FCSTD DOCUMENT  (FreeCAD 0.21R33771 (Git))
Label: MHD-1H
License: All rights reserved
LicenseURL: http://en.wikipedia.org/wiki/All_rights_reserved
objects: Part::Part2DObjectPython×204, App::FeaturePython×31, Part::Feature×23, Part::FeaturePython×14
note: 241 computed .brp shape members not serialized (recipe doc carries the construction recipe); baked Part::Feature solids carry a one-line shape summary decoded from their .brp

FEATURE [Part::Part2DObjectPython] Arc  # Draft 2D object (typed FeaturePython)
  Area = 0
  FirstAngle = -90
  LastAngle = -60.1372
  MakeFace = false
  Placement = pos=(75,95.31,0) rot=(0,0,1;0rad)
  Radius = 75.3125
FEATURE [Part::Part2DObjectPython] Arc001  # Draft 2D object (typed FeaturePython)
  Area = 0
  FirstAngle = -119.863
  LastAngle = -90
  MakeFace = false
  Placement = pos=(-75,95.31,0) rot=(0,0,1;0rad)
  Radius = 75.3125
FEATURE [Part::Part2DObjectPython] Line003  # Draft 2D object (typed FeaturePython)
  Area = 0
  ChamferSize = 0
  Closed = false
  End = (65,-5,0)
  FilletRadius = 0
  Length = 130
  MakeFace = false
  Placement = pos=(-112.523,-5.20498,0) rot=(0,0,1;0rad)
  Points = (2) [(47.5228,0.204983,0),(177.523,0.204983,0)]
  Start = (-65,-5,0)
  Subdivisions = 0
FEATURE [Part::Part2DObjectPython] Line004  # Draft 2D object (typed FeaturePython)
  Area = 0
  ChamferSize = 0
  Closed = false
  End = (75,20,0)
  FilletRadius = 0
  Length = 150
  MakeFace = false
  Placement = pos=(-75,20,0) rot=(0,0,1;0rad)
  Points = (2) [(0,0,0),(150,-7.10543e-15,0)]
  Start = (-75,20,0)
  Subdivisions = 0
FEATURE [Part::Part2DObjectPython] Arc004  # Draft 2D object (typed FeaturePython)
  Area = 0
  FirstAngle = 90
  LastAngle = 119.863
  MakeFace = false
  Placement = pos=(-75,-35.31,0) rot=(0,0,1;0rad)
  Radius = 75.3125
FEATURE [Part::Part2DObjectPython] Arc005  # Draft 2D object (typed FeaturePython)
  Area = 0
  FirstAngle = 60.1372
  LastAngle = 90
  MakeFace = false
  Placement = pos=(75,-35.31,0) rot=(0,0,1;0rad)
  Radius = 75.3125
FEATURE [Part::Part2DObjectPython] Line005  # Draft 2D object (typed FeaturePython)
  Area = 0
  ChamferSize = 0
  Closed = false
  End = (75,40,0)
  FilletRadius = 0
  Length = 150
  MakeFace = false
  Placement = pos=(-75,20,0) rot=(0,0,1;0rad)
  Points = (2) [(0,20,0),(150,20,0)]
  Start = (-75,40,0)
  Subdivisions = 0
FEATURE [Part::Part2DObjectPython] Line006  # Draft 2D object (typed FeaturePython)
  Area = 0
  ChamferSize = 0
  Closed = false
  End = (-142.5,-4.99634,0)
  FilletRadius = 0
  Length = 20
  MakeFace = false
  Placement = pos=(-155.462,-5.16722,0) rot=(0,0,1;0rad)
  Points = (2) [(-7.03764,0.167221,0),(12.9624,0.170881,0)]
  Start = (-162.5,-5,0)
  Subdivisions = 0
FEATURE [Part::Part2DObjectPython] Line010  # Draft 2D object (typed FeaturePython)
  Area = 0
  ChamferSize = 0
  Closed = false
  End = (-152.5,-5,0)
  FilletRadius = 0
  Length = 25
  MakeFace = false
  Points = (2) [(-152.5,-30,0),(-152.5,-5,0)]
  Start = (-152.5,-30,0)
  Subdivisions = 0
FEATURE [Part::Part2DObjectPython] Line020  # Draft 2D object (typed FeaturePython)
  Area = 0
  ChamferSize = 0
  Closed = false
  End = (-71,-39.24,0)
  FilletRadius = 0
  Length = 1
  MakeFace = false
  Placement = pos=(-75,-40,0) rot=(0,0,1;0rad)
  Points = (2) [(3,0.76,0),(4,0.76,0)]
  Start = (-72,-39.24,0)
  Subdivisions = 0
FEATURE [Part::Part2DObjectPython] Line023  # Draft 2D object (typed FeaturePython)
  Area = 0
  ChamferSize = 0
  Closed = false
  End = (-75,-35,0)
  FilletRadius = 0
  Length = 4.5
  MakeFace = false
  Placement = pos=(-75,-40,0) rot=(0,0,1;0rad)
  Points = (2) [(0,0.5,0),(0,5,0)]
  Start = (-75,-39.5,0)
  Subdivisions = 0
FEATURE [Part::Part2DObjectPython] Line024  # Draft 2D object (typed FeaturePython)
  Area = 0
  ChamferSize = 0
  Closed = false
  End = (30,-35,0)
  FilletRadius = 0
  Length = 4.5
  MakeFace = false
  Placement = pos=(-75,-40,0) rot=(0,0,1;0rad)
  Points = (2) [(105,0.5,0),(105,5,0)]
  Start = (30,-39.5,0)
  Subdivisions = 0
FEATURE [Part::Part2DObjectPython] Line028  # Draft 2D object (typed FeaturePython)
  Area = 0
  ChamferSize = 0
  Closed = false
  End = (65,-9.1,0)
  FilletRadius = 0
  Length = 2.2
  MakeFace = false
  Points = (2) [(65,-6.9,0),(65,-9.1,0)]
  Start = (65,-6.9,0)
  Subdivisions = 0
FEATURE [Part::Part2DObjectPython] Line029  # Draft 2D object (typed FeaturePython)
  Area = 0
  ChamferSize = 0
  Closed = false
  End = (36.1,-23,0)
  FilletRadius = 0
  Length = 2.2
  MakeFace = false
  Points = (2) [(33.9,-23,0),(36.1,-23,0)]
  Start = (33.9,-23,0)
  Subdivisions = 0
FEATURE [Part::Part2DObjectPython] Line031  # Draft 2D object (typed FeaturePython)
  Area = 0
  ChamferSize = 0
  Closed = false
  End = (30,20,0)
  FilletRadius = 0
  Length = 20
  MakeFace = false
  Placement = pos=(-75,-40,0) rot=(0,0,1;0rad)
  Points = (2) [(105,80,0),(105,60,0)]
  Start = (30,40,0)
  Subdivisions = 0
FEATURE [Part::Part2DObjectPython] Line032  # Draft 2D object (typed FeaturePython)
  Area = 0
  ChamferSize = 0
  Closed = false
  End = (-65,23.5,0)
  FilletRadius = 0
  Length = 13
  MakeFace = false
  Placement = pos=(-75,-40,0) rot=(0,0,1;0rad)
  Points = (2) [(10,76.5,0),(10,63.5,0)]
  Start = (-65,36.5,0)
  Subdivisions = 0
FEATURE [Part::Part2DObjectPython] Line033  # Draft 2D object (typed FeaturePython)
  Area = 0
  ChamferSize = 0
  Closed = false
  End = (-75,20,0)
  FilletRadius = 0
  Length = 20
  MakeFace = false
  Placement = pos=(-75,-40,0) rot=(0,0,1;0rad)
  Points = (2) [(0,80,0),(0,60,0)]
  Start = (-75,40,0)
  Subdivisions = 0
FEATURE [Part::Part2DObjectPython] Line034  # Draft 2D object (typed FeaturePython)
  Area = 0
  ChamferSize = 0
  Closed = false
  End = (65,23.5,0)
  FilletRadius = 0
  Length = 13
  MakeFace = false
  Placement = pos=(-75,-40,0) rot=(0,0,1;0rad)
  Points = (2) [(140,76.5,0),(140,63.5,0)]
  Start = (65,36.5,0)
  Subdivisions = 0
FEATURE [Part::Part2DObjectPython] Line035  # Draft 2D object (typed FeaturePython)
  Area = 0
  ChamferSize = 0
  Closed = false
  End = (65,36.5,0)
  FilletRadius = 0
  Length = 130
  MakeFace = false
  Placement = pos=(-75,-40,0) rot=(0,0,1;0rad)
  Points = (2) [(10,76.5,0),(140,76.5,0)]
  Start = (-65,36.5,0)
  Subdivisions = 0
FEATURE [Part::Part2DObjectPython] Line036  # Draft 2D object (typed FeaturePython)
  Area = 0
  ChamferSize = 0
  Closed = false
  End = (65,23.5,0)
  FilletRadius = 0
  Length = 130
  MakeFace = false
  Placement = pos=(-75,-40,0) rot=(0,0,1;0rad)
  Points = (2) [(10,63.5,0),(140,63.5,0)]
  Start = (-65,23.5,0)
  Subdivisions = 0
FEATURE [Part::Part2DObjectPython] Line037  # Draft 2D object (typed FeaturePython)
  Area = 0
  ChamferSize = 0
  Closed = false
  End = (75,20,0)
  FilletRadius = 0
  Length = 20
  MakeFace = false
  Placement = pos=(-75,-40,0) rot=(0,0,1;0rad)
  Points = (2) [(150,80,0),(150,60,0)]
  Start = (75,40,0)
  Subdivisions = 0
FEATURE [Part::Part2DObjectPython] Line038  # Draft 2D object (typed FeaturePython)
  Area = 0
  ChamferSize = 0
  Closed = false
  End = (27,23.5,0)
  FilletRadius = 0
  Length = 13.04
  MakeFace = false
  Points = (2) [(27,36.54,0),(27,23.5,0)]
  Start = (27,36.54,0)
  Subdivisions = 0
FEATURE [Part::Part2DObjectPython] Line039  # Draft 2D object (typed FeaturePython)
  Area = 0
  ChamferSize = 0
  Closed = false
  End = (-72,23.5,0)
  FilletRadius = 0
  Length = 13
  MakeFace = false
  Points = (2) [(-72,36.5,0),(-72,23.5,0)]
  Start = (-72,36.5,0)
  Subdivisions = 0
FEATURE [Part::Part2DObjectPython] Line040  # Draft 2D object (typed FeaturePython)
  Area = 0
  ChamferSize = 0
  Closed = false
  End = (-72,23.5,0)
  FilletRadius = 0
  Length = 7
  MakeFace = false
  Placement = pos=(-75,-40,0) rot=(0,0,1;0rad)
  Points = (2) [(10,63.5,0),(3,63.5,0)]
  Start = (-65,23.5,0)
  Subdivisions = 0
FEATURE [Part::Part2DObjectPython] Line041  # Draft 2D object (typed FeaturePython)
  Area = 0
  ChamferSize = 0
  Closed = false
  End = (-72,36.5,0)
  FilletRadius = 0
  Length = 7
  MakeFace = false
  Placement = pos=(-75,-40,0) rot=(0,0,1;0rad)
  Points = (2) [(10,76.5,0),(3,76.5,0)]
  Start = (-65,36.5,0)
  Subdivisions = 0
FEATURE [Part::Part2DObjectPython] Line044  # Draft 2D object (typed FeaturePython)
  Area = 0
  ChamferSize = 0
  Closed = false
  End = (30,39.5,0)
  FilletRadius = 0
  Length = 105
  MakeFace = false
  Placement = pos=(-75,-40,0) rot=(0,0,1;0rad)
  Points = (2) [(0,79.5,0),(105,79.5,0)]
  Start = (-75,39.5,0)
  Subdivisions = 0
FEATURE [Part::Part2DObjectPython] Line045  # Draft 2D object (typed FeaturePython)
  Area = 0
  ChamferSize = 0
  Closed = false
  End = (30,20.5,0)
  FilletRadius = 0
  Length = 105
  MakeFace = false
  Placement = pos=(-75,-40,0) rot=(0,0,1;0rad)
  Points = (2) [(0,60.5,0),(105,60.5,0)]
  Start = (-75,20.5,0)
  Subdivisions = 0
FEATURE [Part::Part2DObjectPython] Line046  # Draft 2D object (typed FeaturePython)
  Area = 0
  ChamferSize = 0
  Closed = false
  End = (30,-35,0)
  FilletRadius = 0
  Length = 105
  MakeFace = false
  Placement = pos=(-75,-40,0) rot=(0,0,1;0rad)
  Points = (2) [(0,5,0),(105,5,0)]
  Start = (-75,-35,0)
  Subdivisions = 0
FEATURE [Part::Part2DObjectPython] Line052  # Draft 2D object (typed FeaturePython)
  Area = 0
  ChamferSize = 0
  Closed = false
  End = (-22,-39.24,0)
  FilletRadius = 0
  Length = 11
  MakeFace = false
  Placement = pos=(-75,-40,0) rot=(0,0,1;0rad)
  Points = (2) [(42,0.76,0),(53,0.76,0)]
  Start = (-33,-39.24,0)
  Subdivisions = 0
FEATURE [Part::Part2DObjectPython] Line053  # Draft 2D object (typed FeaturePython)
  Area = 0
  ChamferSize = 0
  Closed = false
  End = (16,-39.24,0)
  FilletRadius = 0
  Length = 38
  MakeFace = false
  Placement = pos=(-75,-40,0) rot=(0,0,1;0rad)
  Points = (2) [(53,0.76,0),(91,0.76,0)]
  Start = (-22,-39.24,0)
  Subdivisions = 0
FEATURE [Part::Part2DObjectPython] Line054  # Draft 2D object (typed FeaturePython)
  Area = 0
  ChamferSize = 0
  Closed = false
  End = (27,-39.24,0)
  FilletRadius = 0
  Length = 11
  MakeFace = false
  Placement = pos=(-75,-40,0) rot=(0,0,1;0rad)
  Points = (2) [(91,0.76,0),(102,0.76,0)]
  Start = (16,-39.24,0)
  Subdivisions = 0
FEATURE [Part::Part2DObjectPython] Line055  # Draft 2D object (typed FeaturePython)
  Area = 0
  ChamferSize = 0
  Closed = false
  End = (-33,-39.24,0)
  FilletRadius = 0
  Length = 38
  MakeFace = false
  Placement = pos=(-75,-40,0) rot=(0,0,1;0rad)
  Points = (2) [(4,0.76,0),(42,0.76,0)]
  Start = (-71,-39.24,0)
  Subdivisions = 0
FEATURE [Part::Part2DObjectPython] Line064  # Draft 2D object (typed FeaturePython)
  Area = 0
  ChamferSize = 0
  Closed = false
  End = (-146,-23,0)
  FilletRadius = 0
  Length = 13
  MakeFace = false
  Points = (2) [(-159,-23,0),(-146,-23,0)]
  Start = (-159,-23,0)
  Subdivisions = 0
FEATURE [Part::Part2DObjectPython] Line069  # Draft 2D object (typed FeaturePython)
  Area = 0
  ChamferSize = 0
  Closed = false
  End = (-65,-5,0)
  FilletRadius = 0
  Length = 10
  MakeFace = false
  Placement = pos=(-112.523,-5.20498,0) rot=(0,0,1;0rad)
  Points = (2) [(37.5228,0.204983,0),(47.5228,0.204983,0)]
  Start = (-75,-5,0)
  Subdivisions = 0
FEATURE [Part::Part2DObjectPython] Line070  # Draft 2D object (typed FeaturePython)
  Area = 0
  ChamferSize = 0
  Closed = false
  End = (-75,-5.2,0)
  FilletRadius = 0
  Length = 0.2
  MakeFace = false
  Placement = pos=(-112.523,-5.20498,0) rot=(0,0,1;0rad)
  Points = (2) [(37.5228,0.204983,0),(37.5228,0.00498323,0)]
  Start = (-75,-5,0)
  Subdivisions = 0
FEATURE [Part::Part2DObjectPython] Line071  # Draft 2D object (typed FeaturePython)
  Area = 0
  ChamferSize = 0
  Closed = false
  End = (75,-5,0)
  FilletRadius = 0
  Length = 10
  MakeFace = false
  Placement = pos=(-112.523,-5.20498,0) rot=(0,0,1;0rad)
  Points = (2) [(177.523,0.204983,0),(187.523,0.204983,0)]
  Start = (65,-5,0)
  Subdivisions = 0
FEATURE [Part::Part2DObjectPython] Line072  # Draft 2D object (typed FeaturePython)
  Area = 0
  ChamferSize = 0
  Closed = false
  End = (75,-5.2,0)
  FilletRadius = 0
  Length = 0.2
  MakeFace = false
  Placement = pos=(-112.523,-5.20498,0) rot=(0,0,1;0rad)
  Points = (2) [(187.523,0.204983,0),(187.523,0.00498323,0)]
  Start = (75,-5,0)
  Subdivisions = 0
FEATURE [Part::Part2DObjectPython] Line073  # Draft 2D object (typed FeaturePython)
  Area = 0
  ChamferSize = 0
  Closed = false
  End = (-65,-5.2,0)
  FilletRadius = 0
  Length = 0.2
  MakeFace = false
  Points = (2) [(-65,-5,0),(-65,-5.2,0)]
  Start = (-65,-5,0)
  Subdivisions = 0
FEATURE [Part::Part2DObjectPython] Line074  # Draft 2D object (typed FeaturePython)
  Area = 0
  ChamferSize = 0
  Closed = false
  End = (65,-5.2,0)
  FilletRadius = 0
  Length = 0.2
  MakeFace = false
  Points = (2) [(65,-5,0),(65,-5.2,0)]
  Start = (65,-5,0)
  Subdivisions = 0
FEATURE [Part::Part2DObjectPython] Line075  # Draft 2D object (typed FeaturePython)
  Area = 0
  ChamferSize = 0
  Closed = false
  End = (-65,-5.2,0)
  FilletRadius = 0
  Length = 130
  MakeFace = false
  Placement = pos=(-112.523,-5.20498,0) rot=(0,0,1;0rad)
  Points = (2) [(177.523,0.00498323,0),(47.5228,0.00498323,0)]
  Start = (65,-5.2,0)
  Subdivisions = 0
FEATURE [Part::Part2DObjectPython] Line076  # Draft 2D object (typed FeaturePython)
  Area = 0
  ChamferSize = 0
  Closed = true
  End = (-162.5,-5,0)
  FilletRadius = 0
  Length = 30
  MakeFace = false
  Placement = pos=(-112.5,-30,0) rot=(0,0,1;0rad)
  Points = (2) [(-50,25,0),(-50,25,0)]
  Start = (-162.5,-5,0)
  Subdivisions = 0
FEATURE [Part::Part2DObjectPython] Line077  # Draft 2D object (typed FeaturePython)
  Area = 0
  ChamferSize = 0
  Closed = false
  End = (-159,-5,0)
  FilletRadius = 0
  Length = 0.2
  MakeFace = false
  Points = (2) [(-159,-5.2,0),(-159,-5,0)]
  Start = (-159,-5.2,0)
  Subdivisions = 0
FEATURE [Part::Part2DObjectPython] Line078  # Draft 2D object (typed FeaturePython)
  Area = 0
  ChamferSize = 0
  Closed = false
  End = (-146,-5,0)
  FilletRadius = 0
  Length = 0.2
  MakeFace = false
  Points = (2) [(-146,-5.2,0),(-146,-5,0)]
  Start = (-146,-5.2,0)
  Subdivisions = 0
FEATURE [Part::Part2DObjectPython] Line079  # Draft 2D object (typed FeaturePython)
  Area = 0
  ChamferSize = 0
  Closed = false
  End = (-142.5,-5,0)
  FilletRadius = 0
  Length = 0.2
  MakeFace = false
  Placement = pos=(-112.5,-30,0) rot=(0,0,1;0rad)
  Points = (2) [(-30,24.8,0),(-30,25,0)]
  Start = (-142.5,-5.2,0)
  Subdivisions = 0
FEATURE [Part::Part2DObjectPython] Line081  # Draft 2D object (typed FeaturePython)
  Area = 0
  ChamferSize = 0
  Closed = false
  End = (-159,-5.2,0)
  FilletRadius = 0
  Length = 13
  MakeFace = false
  Points = (2) [(-146,-5.2,0),(-159,-5.2,0)]
  Start = (-146,-5.2,0)
  Subdivisions = 0
FEATURE [Part::Part2DObjectPython] Line083  # Draft 2D object (typed FeaturePython)
  Area = 0
  ChamferSize = 0
  Closed = true
  End = (-71,35.5,0)
  FilletRadius = 0
  Length = 11
  MakeFace = false
  Placement = pos=(-157.5,-40,0) rot=(0,0,1;0rad)
  Points = (2) [(86.5,64.5,0),(86.5,75.5,0)]
  Start = (-71,24.5,0)
  Subdivisions = 0
FEATURE [Part::Part2DObjectPython] Line084  # Draft 2D object (typed FeaturePython)
  Area = 0
  ChamferSize = 0
  Closed = true
  End = (-33,35.5,0)
  FilletRadius = 0
  Length = 11
  MakeFace = false
  Placement = pos=(-157.5,-40,0) rot=(0,0,1;0rad)
  Points = (2) [(124.5,64.5,0),(124.5,75.5,0)]
  Start = (-33,24.5,0)
  Subdivisions = 0
FEATURE [Part::Part2DObjectPython] Line087  # Draft 2D object (typed FeaturePython)
  Area = 0
  ChamferSize = 0
  Closed = false
  End = (-33,35.5,0)
  FilletRadius = 0
  Length = 32
  MakeFace = false
  Placement = pos=(-70.9707,35.5939,0) rot=(0,0,1;0rad)
  Points = (2) [(5.97074,-0.0939102,0),(37.9707,-0.0939102,0)]
  Start = (-65,35.5,0)
  Subdivisions = 0
FEATURE [Part::Part2DObjectPython] Line088  # Draft 2D object (typed FeaturePython)
  Area = 0
  ChamferSize = 0
  Closed = false
  End = (-65,35.5,0)
  FilletRadius = 0
  Length = 6
  MakeFace = false
  Placement = pos=(-70.9707,35.5939,0) rot=(0,0,1;0rad)
  Points = (2) [(-0.0292587,-0.0939102,0),(5.97074,-0.0939102,0)]
  Start = (-71,35.5,0)
  Subdivisions = 0
FEATURE [Part::Part2DObjectPython] Line089  # Draft 2D object (typed FeaturePython)
  Area = 0
  ChamferSize = 0
  Closed = false
  End = (-65,24.5,0)
  FilletRadius = 0
  Length = 6
  MakeFace = false
  Placement = pos=(-70.9707,35.5939,0) rot=(0,0,1;0rad)
  Points = (2) [(-0.0292587,-11.0939,0),(5.97074,-11.0939,0)]
  Start = (-71,24.5,0)
  Subdivisions = 0
FEATURE [Part::Part2DObjectPython] Line090  # Draft 2D object (typed FeaturePython)
  Area = 0
  ChamferSize = 0
  Closed = false
  End = (-33,24.5,0)
  FilletRadius = 0
  Length = 32
  MakeFace = false
  Placement = pos=(-70.9707,35.5939,0) rot=(0,0,1;0rad)
  Points = (2) [(5.97074,-11.0939,0),(37.9707,-11.0939,0)]
  Start = (-65,24.5,0)
  Subdivisions = 0
FEATURE [Part::Part2DObjectPython] Line095  # Draft 2D object (typed FeaturePython)
  Area = 0
  ChamferSize = 0
  Closed = true
  End = (35.5,-23,0)
  FilletRadius = 0
  Length = 35.4
  MakeFace = false
  Placement = pos=(35.5,-60,0) rot=(0,0,1;0rad)
  Points = (2) [(0,1.6,0),(0,37,0)]
  Start = (35.5,-58.4,0)
  Subdivisions = 0
FEATURE [Part::Part2DObjectPython] Line096  # Draft 2D object (typed FeaturePython)
  Area = 0
  ChamferSize = 0
  Closed = false
  End = (74.5,-18,0)
  FilletRadius = 0
  Length = 40.4
  MakeFace = false
  Placement = pos=(35.5,-60,0) rot=(0,0,1;0rad)
  Points = (2) [(39,1.6,0),(39,42,0)]
  Start = (74.5,-58.4,0)
  Subdivisions = 0
FEATURE [Part::Part2DObjectPython] Line097  # Draft 2D object (typed FeaturePython)
  Area = 0
  ChamferSize = 0
  Closed = true
  End = (35,-62.2,0)
  FilletRadius = 0
  Length = 0.5
  MakeFace = false
  Placement = pos=(35.5,-60,0) rot=(0,0,1;0rad)
  Points = (2) [(0,-2.2,0),(-0.5,-2.2,0)]
  Start = (35.5,-62.2,0)
  Subdivisions = 0
FEATURE [Part::Part2DObjectPython] Line099  # Draft 2D object (typed FeaturePython)
  Area = 0
  ChamferSize = 0
  Closed = true
  End = (75.5,-18,0)
  FilletRadius = 0
  Length = 43.7
  MakeFace = false
  Placement = pos=(35.5,-60,0) rot=(0,0,1;0rad)
  Points = (2) [(40,-1.7,0),(40,42,0)]
  Start = (75.5,-61.7,0)
  Subdivisions = 0
FEATURE [Part::Part2DObjectPython] Line101  # Draft 2D object (typed FeaturePython)
  Area = 0
  ChamferSize = 0
  Closed = true
  End = (35.5,-62.2,0)
  FilletRadius = 0
  Length = 37
  MakeFace = false
  Placement = pos=(35.5,-60,0) rot=(0,0,1;0rad)
  Points = (2) [(37,-2.2,0),(0,-2.2,0)]
  Start = (72.5,-62.2,0)
  Subdivisions = 0
FEATURE [Part::Part2DObjectPython] Line102  # Draft 2D object (typed FeaturePython)
  Area = 0
  ChamferSize = 0
  Closed = true
  End = (34.5,-23,0)
  FilletRadius = 0
  Length = 38.7
  MakeFace = false
  Placement = pos=(35.5,-60,0) rot=(0,0,1;0rad)
  Points = (2) [(-1,-1.7,0),(-1,37,0)]
  Start = (34.5,-61.7,0)
  Subdivisions = 0
FEATURE [Part::Part2DObjectPython] Arc010  # Draft 2D object (typed FeaturePython)
  Area = 0
  FirstAngle = 0
  LastAngle = 90
  MakeFace = false
  Placement = pos=(27,-23,0) rot=(0,0,1;0rad)
  Radius = 6.9
FEATURE [Part::Part2DObjectPython] Arc011  # Draft 2D object (typed FeaturePython)
  Area = 0
  FirstAngle = 0
  LastAngle = 90
  MakeFace = false
  Placement = pos=(65,-18,0) rot=(0,0,1;0rad)
  Radius = 9.5
FEATURE [Part::Part2DObjectPython] Arc012  # Draft 2D object (typed FeaturePython)
  Area = 0
  FirstAngle = 0
  LastAngle = 90
  MakeFace = false
  Placement = pos=(65,-18,0) rot=(0,0,1;0rad)
  Radius = 10.5
FEATURE [Part::Part2DObjectPython] Arc015  # Draft 2D object (typed FeaturePython)
  Area = 0
  FirstAngle = 0
  LastAngle = 90
  MakeFace = false
  Placement = pos=(27,-23,0) rot=(0,0,1;0rad)
  Radius = 7.5
FEATURE [Part::Part2DObjectPython] Arc016  # Draft 2D object (typed FeaturePython)
  Area = 0
  FirstAngle = 0
  LastAngle = 90
  MakeFace = false
  Placement = pos=(27,-23,0) rot=(0,0,1;0rad)
  Radius = 8.5
FEATURE [Part::Part2DObjectPython] Arc017  # Draft 2D object (typed FeaturePython)
  Area = 0
  FirstAngle = 0
  LastAngle = 90
  MakeFace = false
  Placement = pos=(27,-23,0) rot=(0,0,1;0rad)
  Radius = 9.1
FEATURE [Part::Part2DObjectPython] Arc018  # Draft 2D object (typed FeaturePython)
  Area = 0
  FirstAngle = 90
  LastAngle = 180
  MakeFace = false
  Placement = pos=(35,-61.7,0) rot=(0,0,1;0rad)
  Radius = 0.5
FEATURE [Part::Part2DObjectPython] Arc019  # Draft 2D object (typed FeaturePython)
  Area = 0
  FirstAngle = 180
  LastAngle = 360
  MakeFace = false
  Placement = pos=(35,-61.7,0) rot=(0,0,1;0rad)
  Radius = 0.5
FEATURE [Part::Part2DObjectPython] Line105  # Draft 2D object (typed FeaturePython)
  Area = 0
  ChamferSize = 0
  Closed = true
  End = (35,-61.2,0)
  FilletRadius = 0
  Length = 37.5
  MakeFace = false
  Placement = pos=(35.5,-60,0) rot=(0,0,1;0rad)
  Points = (2) [(37,-1.2,0),(-0.5,-1.2,0)]
  Start = (72.5,-61.2,0)
  Subdivisions = 0
FEATURE [Part::Part2DObjectPython] Line106  # Draft 2D object (typed FeaturePython)
  Area = 0
  ChamferSize = 0
  Closed = true
  End = (71.5,-61.2,0)
  FilletRadius = 0
  Length = 1
  MakeFace = false
  Placement = pos=(35.5,-60,0) rot=(0,0,1;0rad)
  Points = (2) [(36,-2.2,0),(36,-1.2,0)]
  Start = (71.5,-62.2,0)
  Subdivisions = 0
FEATURE [Part::Part2DObjectPython] Arc020  # Draft 2D object (typed FeaturePython)
  Area = 0
  FirstAngle = 180
  LastAngle = 360
  MakeFace = false
  Placement = pos=(75,-61.7,0) rot=(0,0,1;0rad)
  Radius = 0.5
FEATURE [Part::Part2DObjectPython] Line107  # Draft 2D object (typed FeaturePython)
  Area = 0
  ChamferSize = 0
  Closed = true
  End = (72.5,-58.7,0)
  FilletRadius = 0
  Length = 6
  MakeFace = false
  Placement = pos=(35.5,-60,0) rot=(0,0,1;0rad)
  Points = (2) [(37,-4.7,0),(37,1.3,0)]
  Start = (72.5,-64.7,0)
  Subdivisions = 0
FEATURE [Part::Part2DObjectPython] Line108  # Draft 2D object (typed FeaturePython)
  Area = 0
  ChamferSize = 0
  Closed = true
  End = (37.5,-58.7,0)
  FilletRadius = 0
  Length = 6
  MakeFace = false
  Placement = pos=(35.5,-60,0) rot=(0,0,1;0rad)
  Points = (2) [(2,-4.7,0),(2,1.3,0)]
  Start = (37.5,-64.7,0)
  Subdivisions = 0
FEATURE [Part::Part2DObjectPython] Line109  # Draft 2D object (typed FeaturePython)
  Area = 0
  ChamferSize = 0
  Closed = true
  End = (37.5,-58.7,0)
  FilletRadius = 0
  Length = 35
  MakeFace = false
  Placement = pos=(35.5,-60,0) rot=(0,0,1;0rad)
  Points = (2) [(37,1.3,0),(2,1.3,0)]
  Start = (72.5,-58.7,0)
  Subdivisions = 0
FEATURE [Part::Part2DObjectPython] Line110  # Draft 2D object (typed FeaturePython)
  Area = 0
  ChamferSize = 0
  Closed = true
  End = (37.5,-64.7,0)
  FilletRadius = 0
  Length = 35
  MakeFace = false
  Placement = pos=(35.5,-60,0) rot=(0,0,1;0rad)
  Points = (2) [(37,-4.7,0),(2,-4.7,0)]
  Start = (72.5,-64.7,0)
  Subdivisions = 0
FEATURE [Part::Part2DObjectPython] Arc021  # Draft 2D object (typed FeaturePython)
  Area = 0
  FirstAngle = -90
  LastAngle = -89.1631
  MakeFace = false
  Placement = pos=(75,35.31,0) rot=(0,0,1;0rad)
  Radius = 75.3125
  expr: LastAngle = -89.16312 °
FEATURE [Part::Part2DObjectPython] Line111  # Draft 2D object (typed FeaturePython)
  Area = 0
  ChamferSize = 0
  Closed = false
  End = (73.9,-40,0)
  FilletRadius = 0
  Length = 1.1
  MakeFace = false
  Placement = pos=(-75,-40,0) rot=(0,0,1;0rad)
  Points = (2) [(150,0,0),(148.9,0,0)]
  Start = (75,-40,0)
  Subdivisions = 0
FEATURE [Part::Part2DObjectPython] Line113  # Draft 2D object (typed FeaturePython)
  Area = 0
  ChamferSize = 0
  Closed = false
  End = (36.1,-40,0)
  FilletRadius = 0
  Length = 2.2
  MakeFace = false
  Placement = pos=(-75,-40,0) rot=(0,0,1;0rad)
  Points = (2) [(108.9,0,0),(111.1,0,0)]
  Start = (33.9,-40,0)
  Subdivisions = 0
FEATURE [Part::Part2DObjectPython] Line116  # Draft 2D object (typed FeaturePython)
  Area = 0
  ChamferSize = 0
  Closed = false
  End = (62,31.1,0)
  FilletRadius = 0
  Length = 2.2
  MakeFace = false
  Points = (2) [(62,28.9,0),(62,31.1,0)]
  Start = (62,28.9,0)
  Subdivisions = 0
FEATURE [Part::Part2DObjectPython] Line117  # Draft 2D object (typed FeaturePython)
  Area = 0
  ChamferSize = 0
  Closed = false
  End = (65,-9.1,0)
  FilletRadius = 0
  Length = 3
  MakeFace = false
  Points = (2) [(62,-9.1,0),(65,-9.1,0)]
  Start = (62,-9.1,0)
  Subdivisions = 0
FEATURE [Part::Part2DObjectPython] Line120  # Draft 2D object (typed FeaturePython)
  Area = 0
  ChamferSize = 0
  Closed = false
  End = (62,-8.5,0)
  FilletRadius = 0
  Length = 1
  MakeFace = false
  Points = (2) [(62,-7.5,0),(62,-8.5,0)]
  Start = (62,-7.5,0)
  Subdivisions = 0
FEATURE [Part::Part2DObjectPython] Line121  # Draft 2D object (typed FeaturePython)
  Area = 0
  ChamferSize = 0
  Closed = false
  End = (23,-15.5,0)
  FilletRadius = 0
  Length = 4
  MakeFace = false
  Points = (2) [(27,-15.5,0),(23,-15.5,0)]
  Start = (27,-15.5,0)
  Subdivisions = 0
FEATURE [Part::Part2DObjectPython] Line122  # Draft 2D object (typed FeaturePython)
  Area = 0
  ChamferSize = 0
  Closed = false
  End = (65,-7.5,0)
  FilletRadius = 0
  Length = 7
  MakeFace = false
  Points = (2) [(58,-7.5,0),(65,-7.5,0)]
  Start = (58,-7.5,0)
  Subdivisions = 0
FEATURE [Part::Part2DObjectPython] Line123  # Draft 2D object (typed FeaturePython)
  Area = 0
  ChamferSize = 0
  Closed = false
  End = (58,29.5,0)
  FilletRadius = 0
  Length = 1
  MakeFace = false
  Points = (2) [(58,30.5,0),(58,29.5,0)]
  Start = (58,30.5,0)
  Subdivisions = 0
FEATURE [Part::Part2DObjectPython] Line124  # Draft 2D object (typed FeaturePython)
  Area = 0
  ChamferSize = 0
  Closed = false
  End = (62,-9.1,0)
  FilletRadius = 0
  Length = 0.6
  MakeFace = false
  Points = (2) [(62,-8.5,0),(62,-9.1,0)]
  Start = (62,-8.5,0)
  Subdivisions = 0
FEATURE [Part::Part2DObjectPython] Line125  # Draft 2D object (typed FeaturePython)
  Area = 0
  ChamferSize = 0
  Closed = false
  End = (62,-7.5,0)
  FilletRadius = 0
  Length = 0.6
  MakeFace = false
  Points = (2) [(62,-6.9,0),(62,-7.5,0)]
  Start = (62,-6.9,0)
  Subdivisions = 0
FEATURE [Part::Part2DObjectPython] Line126  # Draft 2D object (typed FeaturePython)
  Area = 0
  ChamferSize = 0
  Closed = false
  End = (65,-8.5,0)
  FilletRadius = 0
  Length = 7
  MakeFace = false
  Points = (2) [(58,-8.5,0),(65,-8.5,0)]
  Start = (58,-8.5,0)
  Subdivisions = 0
FEATURE [Part::Part2DObjectPython] Line127  # Draft 2D object (typed FeaturePython)
  Area = 0
  ChamferSize = 0
  Closed = false
  End = (23,-14.5,0)
  FilletRadius = 0
  Length = 4
  MakeFace = false
  Points = (2) [(27,-14.5,0),(23,-14.5,0)]
  Start = (27,-14.5,0)
  Subdivisions = 0
FEATURE [Part::Part2DObjectPython] Line128  # Draft 2D object (typed FeaturePython)
  Area = 0
  ChamferSize = 0
  Closed = false
  End = (23,-14.5,0)
  FilletRadius = 0
  Length = 1
  MakeFace = false
  Points = (2) [(23,-15.5,0),(23,-14.5,0)]
  Start = (23,-15.5,0)
  Subdivisions = 0
FEATURE [Part::Part2DObjectPython] Line129  # Draft 2D object (typed FeaturePython)
  Area = 0
  ChamferSize = 0
  Closed = false
  End = (23,-14.5,0)
  FilletRadius = 0
  Length = 4
  MakeFace = false
  Points = (2) [(27,-14.5,0),(23,-14.5,0)]
  Start = (27,-14.5,0)
  Subdivisions = 0
FEATURE [Part::Part2DObjectPython] Line130  # Draft 2D object (typed FeaturePython)
  Area = 0
  ChamferSize = 0
  Closed = false
  End = (27,-14.5,0)
  FilletRadius = 0
  Length = 1
  MakeFace = false
  Points = (2) [(27,-15.5,0),(27,-14.5,0)]
  Start = (27,-15.5,0)
  Subdivisions = 0
FEATURE [Part::Part2DObjectPython] Line131  # Draft 2D object (typed FeaturePython)
  Area = 0
  ChamferSize = 0
  Closed = false
  End = (27,-14.5,0)
  FilletRadius = 0
  Length = 0.6
  MakeFace = false
  Points = (2) [(27,-13.9,0),(27,-14.5,0)]
  Start = (27,-13.9,0)
  Subdivisions = 0
FEATURE [Part::Part2DObjectPython] Line132  # Draft 2D object (typed FeaturePython)
  Area = 0
  ChamferSize = 0
  Closed = false
  End = (27,-16.1,0)
  FilletRadius = 0
  Length = 0.6
  MakeFace = false
  Points = (2) [(27,-15.5,0),(27,-16.1,0)]
  Start = (27,-15.5,0)
  Subdivisions = 0
FEATURE [Part::Part2DObjectPython] Line134  # Draft 2D object (typed FeaturePython)
  Area = 0
  ChamferSize = 0
  Closed = true
  End = (-153,-58.4,0)
  FilletRadius = 0
  Length = 2.8
  MakeFace = false
  Placement = pos=(35.5,-60,0) rot=(0,0,1;0rad)
  Points = (2) [(-188.5,-1.2,0),(-188.5,1.6,0)]
  Start = (-153,-61.2,0)
  Subdivisions = 0
FEATURE [Part::Part2DObjectPython] Line135  # Draft 2D object (typed FeaturePython)
  Area = 0
  ChamferSize = 0
  Closed = true
  End = (-152,-8,0)
  FilletRadius = 0
  Length = 50.4
  MakeFace = false
  Placement = pos=(35.5,-60,0) rot=(0,0,1;0rad)
  Points = (2) [(-187.5,1.6,0),(-187.5,52,0)]
  Start = (-152,-58.4,0)
  Subdivisions = 0
FEATURE [Part::Part2DObjectPython] Line136  # Draft 2D object (typed FeaturePython)
  Area = 0
  ChamferSize = 0
  Closed = false
  End = (-149.2,-65,0)
  FilletRadius = 0
  Length = 6.6
  MakeFace = false
  Placement = pos=(35.5,-60,0) rot=(0,0,1;0rad)
  Points = (2) [(-191.3,-5,0),(-184.7,-5,0)]
  Start = (-155.8,-65,0)
  Subdivisions = 0
FEATURE [Part::Part2DObjectPython] Line138  # Draft 2D object (typed FeaturePython)
  Area = 0
  ChamferSize = 0
  Closed = true
  End = (-155.8,-58.4,0)
  FilletRadius = 0
  Length = 2.8
  MakeFace = false
  Placement = pos=(35.5,-60,0) rot=(0,0,1;0rad)
  Points = (2) [(-191.3,-1.2,0),(-191.3,1.6,0)]
  Start = (-155.8,-61.2,0)
  Subdivisions = 0
FEATURE [Part::Part2DObjectPython] Line139  # Draft 2D object (typed FeaturePython)
  Area = 0
  ChamferSize = 0
  Closed = false
  End = (-149.2,-58.4,0)
  FilletRadius = 0
  Length = 6.6
  MakeFace = false
  Placement = pos=(35.5,-60,0) rot=(0,0,1;0rad)
  Points = (2) [(-184.7,-5,0),(-184.7,1.6,0)]
  Start = (-149.2,-65,0)
  Subdivisions = 0
FEATURE [Part::Part2DObjectPython] Line140  # Draft 2D object (typed FeaturePython)
  Area = 0
  ChamferSize = 0
  Closed = false
  End = (-149.2,-58.4,0)
  FilletRadius = 0
  Length = 6.6
  MakeFace = false
  Placement = pos=(35.5,-60,0) rot=(0,0,1;0rad)
  Points = (2) [(-191.3,1.6,0),(-184.7,1.6,0)]
  Start = (-155.8,-58.4,0)
  Subdivisions = 0
FEATURE [Part::Part2DObjectPython] Line142  # Draft 2D object (typed FeaturePython)
  Area = 0
  ChamferSize = 0
  Closed = true
  End = (-151.4,-40,0)
  FilletRadius = 0
  Length = 18.4
  MakeFace = false
  Placement = pos=(35.5,-60,0) rot=(0,0,1;0rad)
  Points = (2) [(-186.9,1.6,0),(-186.9,20,0)]
  Start = (-151.4,-58.4,0)
  Subdivisions = 0
FEATURE [Part::Part2DObjectPython] Line143  # Draft 2D object (typed FeaturePython)
  Area = 0
  ChamferSize = 0
  Closed = true
  End = (-152,-58.4,0)
  FilletRadius = 0
  Length = 3.3
  MakeFace = false
  Placement = pos=(35.5,-60,0) rot=(0,0,1;0rad)
  Points = (2) [(-187.5,-1.7,0),(-187.5,1.6,0)]
  Start = (-152,-61.7,0)
  Subdivisions = 0
FEATURE [Part::Part2DObjectPython] Line144  # Draft 2D object (typed FeaturePython)
  Area = 0
  ChamferSize = 0
  Closed = true
  End = (-153,-8,0)
  FilletRadius = 0
  Length = 50.4
  MakeFace = false
  Placement = pos=(35.5,-60,0) rot=(0,0,1;0rad)
  Points = (2) [(-188.5,1.6,0),(-188.5,52,0)]
  Start = (-153,-58.4,0)
  Subdivisions = 0
FEATURE [Part::Part2DObjectPython] Line145  # Draft 2D object (typed FeaturePython)
  Area = 0
  ChamferSize = 0
  Closed = true
  End = (-153.6,-23,0)
  FilletRadius = 0
  Length = 17
  MakeFace = false
  Placement = pos=(35.5,-60,0) rot=(0,0,1;0rad)
  Points = (2) [(-189.1,20,0),(-189.1,37,0)]
  Start = (-153.6,-40,0)
  Subdivisions = 0
FEATURE [Part::Part2DObjectPython] Line146  # Draft 2D object (typed FeaturePython)
  Area = 0
  ChamferSize = 0
  Closed = true
  End = (-153.6,-40,0)
  FilletRadius = 0
  Length = 18.4
  MakeFace = false
  Placement = pos=(35.5,-60,0) rot=(0,0,1;0rad)
  Points = (2) [(-189.1,1.6,0),(-189.1,20,0)]
  Start = (-153.6,-58.4,0)
  Subdivisions = 0
FEATURE [Part::Part2DObjectPython] Line147  # Draft 2D object (typed FeaturePython)
  Area = 0
  ChamferSize = 0
  Closed = true
  End = (-151.4,-23,0)
  FilletRadius = 0
  Length = 17
  MakeFace = false
  Placement = pos=(35.5,-60,0) rot=(0,0,1;0rad)
  Points = (2) [(-186.9,20,0),(-186.9,37,0)]
  Start = (-151.4,-40,0)
  Subdivisions = 0
FEATURE [Part::Part2DObjectPython] Circle  # Draft 2D object (typed FeaturePython)
  Area = 0
  FirstAngle = 0
  LastAngle = 0
  MakeFace = false
  Placement = pos=(-152.5,-8,0) rot=(0,0,1;0rad)
  Radius = 0.5
FEATURE [Part::Part2DObjectPython] Circle001  # Draft 2D object (typed FeaturePython)
  Area = 0
  FirstAngle = 0
  LastAngle = 0
  MakeFace = false
  Placement = pos=(-152.5,-8,0) rot=(0,0,1;0rad)
  Radius = 1.1
FEATURE [Part::Part2DObjectPython] Circle002  # Draft 2D object (typed FeaturePython)
  Area = 0
  FirstAngle = 0
  LastAngle = 0
  MakeFace = false
  Placement = pos=(-152.5,-15,0) rot=(0,0,1;0rad)
  Radius = 0.5
FEATURE [Part::Part2DObjectPython] Circle003  # Draft 2D object (typed FeaturePython)
  Area = 0
  FirstAngle = 0
  LastAngle = 0
  MakeFace = false
  Placement = pos=(-152.5,-15,0) rot=(0,0,1;0rad)
  Radius = 1.1
FEATURE [Part::Part2DObjectPython] Line148  # Draft 2D object (typed FeaturePython)
  Area = 0
  ChamferSize = 0
  Closed = true
  End = (-151.4,-8,0)
  FilletRadius = 0
  Length = 15
  MakeFace = false
  Placement = pos=(35.5,-60,0) rot=(0,0,1;0rad)
  Points = (2) [(-186.9,37,0),(-186.9,52,0)]
  Start = (-151.4,-23,0)
  Subdivisions = 0
FEATURE [Part::Part2DObjectPython] Line149  # Draft 2D object (typed FeaturePython)
  Area = 0
  ChamferSize = 0
  Closed = true
  End = (-153.6,-8,0)
  FilletRadius = 0
  Length = 15
  MakeFace = false
  Placement = pos=(35.5,-60,0) rot=(0,0,1;0rad)
  Points = (2) [(-189.1,37,0),(-189.1,52,0)]
  Start = (-153.6,-23,0)
  Subdivisions = 0
FEATURE [Part::Part2DObjectPython] Line150  # Draft 2D object (typed FeaturePython)
  Area = 0
  ChamferSize = 0
  Closed = true
  End = (-156.8,-61.2,0)
  FilletRadius = 0
  Length = 0.9
  MakeFace = false
  Placement = pos=(35.5,-60,0) rot=(0,0,1;0rad)
  Points = (2) [(-191.4,-1.2,0),(-192.3,-1.2,0)]
  Start = (-155.9,-61.2,0)
  Subdivisions = 0
FEATURE [Part::Part2DObjectPython] Line151  # Draft 2D object (typed FeaturePython)
  Area = 0
  ChamferSize = 0
  Closed = true
  End = (-155.9,-62.2,0)
  FilletRadius = 0
  Length = 0.9
  MakeFace = false
  Placement = pos=(35.5,-60,0) rot=(0,0,1;0rad)
  Points = (2) [(-192.3,-2.2,0),(-191.4,-2.2,0)]
  Start = (-156.8,-62.2,0)
  Subdivisions = 0
FEATURE [Part::Part2DObjectPython] Arc022  # Draft 2D object (typed FeaturePython)
  Area = 0
  FirstAngle = -180
  LastAngle = 0
  MakeFace = false
  Placement = pos=(-152.5,-61.7,0) rot=(0,0,1;0rad)
  Radius = 0.5
FEATURE [Part::Part2DObjectPython] Arc023  # Draft 2D object (typed FeaturePython)
  Area = 0
  FirstAngle = -90
  LastAngle = 90
  MakeFace = false
  Placement = pos=(-156.3,-61.7,0) rot=(0,0,1;0rad)
  Radius = 0.5
FEATURE [Part::Part2DObjectPython] Arc024  # Draft 2D object (typed FeaturePython)
  Area = 0
  FirstAngle = 90
  LastAngle = 270
  MakeFace = false
  Placement = pos=(-156.3,-61.7,0) rot=(0,0,1;0rad)
  Radius = 0.5
FEATURE [Part::Part2DObjectPython] Line152  # Draft 2D object (typed FeaturePython)
  Area = 0
  ChamferSize = 0
  Closed = true
  End = (-156.8,-61.2,0)
  FilletRadius = 0
  Length = 1
  MakeFace = false
  Placement = pos=(35.5,-60,0) rot=(0,0,1;0rad)
  Points = (2) [(-192.3,-2.2,0),(-192.3,-1.2,0)]
  Start = (-156.8,-62.2,0)
  Subdivisions = 0
FEATURE [Part::Part2DObjectPython] Circle004  # Draft 2D object (typed FeaturePython)
  Area = 0
  FirstAngle = 0
  LastAngle = 0
  MakeFace = false
  Placement = pos=(-148.7,-61.7,0) rot=(0,0,1;0rad)
  Radius = 0.5
FEATURE [Part::Part2DObjectPython] Line153  # Draft 2D object (typed FeaturePython)
  Area = 0
  ChamferSize = 0
  Closed = true
  End = (-149.1,-61.2,0)
  FilletRadius = 0
  Length = 0.9
  MakeFace = false
  Placement = pos=(35.5,-60,0) rot=(0,0,1;0rad)
  Points = (2) [(-183.7,-1.2,0),(-184.6,-1.2,0)]
  Start = (-148.2,-61.2,0)
  Subdivisions = 0
FEATURE [Part::Part2DObjectPython] Line154  # Draft 2D object (typed FeaturePython)
  Area = 0
  ChamferSize = 0
  Closed = true
  End = (-149.1,-62.2,0)
  FilletRadius = 0
  Length = 0.9
  MakeFace = false
  Placement = pos=(35.5,-60,0) rot=(0,0,1;0rad)
  Points = (2) [(-183.7,-2.2,0),(-184.6,-2.2,0)]
  Start = (-148.2,-62.2,0)
  Subdivisions = 0
FEATURE [Part::Part2DObjectPython] Line155  # Draft 2D object (typed FeaturePython)
  Area = 0
  ChamferSize = 0
  Closed = true
  End = (-148.2,-62.2,0)
  FilletRadius = 0
  Length = 1
  MakeFace = false
  Placement = pos=(35.5,-60,0) rot=(0,0,1;0rad)
  Points = (2) [(-183.7,-1.2,0),(-183.7,-2.2,0)]
  Start = (-148.2,-61.2,0)
  Subdivisions = 0
FEATURE [Part::Part2DObjectPython] Arc025  # Draft 2D object (typed FeaturePython)
  Area = 0
  FirstAngle = -58.9973
  LastAngle = 58.9973
  MakeFace = false
  Placement = pos=(-150.6,-61.7,0) rot=(0,0,1;0rad)
  Radius = 3.5
FEATURE [Part::Part2DObjectPython] Arc026  # Draft 2D object (typed FeaturePython)
  Area = 0
  FirstAngle = 121.003
  LastAngle = 238.997
  MakeFace = false
  Placement = pos=(-154.4,-61.7,0) rot=(0,0,1;0rad)
  Radius = 3.5
FEATURE [Part::Part2DObjectPython] Line156  # Draft 2D object (typed FeaturePython)
  Area = 0
  ChamferSize = 0
  Closed = false
  End = (-149.1,-58.7,0)
  FilletRadius = 0
  Length = 2.5
  MakeFace = false
  Placement = pos=(35.5,-60,0) rot=(0,0,1;0rad)
  Points = (2) [(-184.6,-1.2,0),(-184.6,1.3,0)]
  Start = (-149.1,-61.2,0)
  Subdivisions = 0
FEATURE [Part::Part2DObjectPython] Line157  # Draft 2D object (typed FeaturePython)
  Area = 0
  ChamferSize = 0
  Closed = false
  End = (-155.9,-58.7,0)
  FilletRadius = 0
  Length = 2.5
  MakeFace = false
  Placement = pos=(35.5,-60,0) rot=(0,0,1;0rad)
  Points = (2) [(-191.4,-1.2,0),(-191.4,1.3,0)]
  Start = (-155.9,-61.2,0)
  Subdivisions = 0
FEATURE [Part::Part2DObjectPython] Line158  # Draft 2D object (typed FeaturePython)
  Area = 0
  ChamferSize = 0
  Closed = false
  End = (-155.9,-62.2,0)
  FilletRadius = 0
  Length = 2.5
  MakeFace = false
  Placement = pos=(35.5,-60,0) rot=(0,0,1;0rad)
  Points = (2) [(-191.4,-4.7,0),(-191.4,-2.2,0)]
  Start = (-155.9,-64.7,0)
  Subdivisions = 0
FEATURE [Part::Part2DObjectPython] Line159  # Draft 2D object (typed FeaturePython)
  Area = 0
  ChamferSize = 0
  Closed = false
  End = (-149.1,-62.2,0)
  FilletRadius = 0
  Length = 2.5
  MakeFace = false
  Placement = pos=(35.5,-60,0) rot=(0,0,1;0rad)
  Points = (2) [(-184.6,-4.7,0),(-184.6,-2.2,0)]
  Start = (-149.1,-64.7,0)
  Subdivisions = 0
FEATURE [Part::Part2DObjectPython] Line160  # Draft 2D object (typed FeaturePython)
  Area = 0
  ChamferSize = 0
  Closed = true
  End = (-155.9,-61.2,0)
  FilletRadius = 0
  Length = 2.9
  MakeFace = false
  Placement = pos=(35.5,-60,0) rot=(0,0,1;0rad)
  Points = (2) [(-188.5,-1.2,0),(-191.4,-1.2,0)]
  Start = (-153,-61.2,0)
  Subdivisions = 0
FEATURE [Part::Part2DObjectPython] Line161  # Draft 2D object (typed FeaturePython)
  Area = 0
  ChamferSize = 0
  Closed = true
  End = (-155.9,-62.2,0)
  FilletRadius = 0
  Length = 3.4
  MakeFace = false
  Placement = pos=(35.5,-60,0) rot=(0,0,1;0rad)
  Points = (2) [(-188,-2.2,0),(-191.4,-2.2,0)]
  Start = (-152.5,-62.2,0)
  Subdivisions = 0
FEATURE [Part::Part2DObjectPython] Line162  # Draft 2D object (typed FeaturePython)
  Area = 0
  ChamferSize = 0
  Closed = true
  End = (-155.8,-61.2,0)
  FilletRadius = 0
  Length = 1
  MakeFace = false
  Placement = pos=(35.5,-60,0) rot=(0,0,1;0rad)
  Points = (2) [(-191.3,-2.2,0),(-191.3,-1.2,0)]
  Start = (-155.8,-62.2,0)
  Subdivisions = 0
FEATURE [Part::Part2DObjectPython] Line163  # Draft 2D object (typed FeaturePython)
  Area = 0
  ChamferSize = 0
  Closed = true
  End = (-155.8,-62.2,0)
  FilletRadius = 0
  Length = 2.8
  MakeFace = false
  Placement = pos=(35.5,-60,0) rot=(0,0,1;0rad)
  Points = (2) [(-191.3,-5,0),(-191.3,-2.2,0)]
  Start = (-155.8,-65,0)
  Subdivisions = 0
FEATURE [Part::Part2DObjectPython] Arc027  # Draft 2D object (typed FeaturePython)
  Area = 0
  FirstAngle = -90
  LastAngle = 0
  MakeFace = false
  Placement = pos=(-152.5,-61.7,0) rot=(0,0,1;0rad)
  Radius = 0.5
FEATURE [Part::Part2DObjectPython] Line164  # Draft 2D object (typed FeaturePython)
  Area = 0
  ChamferSize = 0
  Closed = true
  End = (-153,-61.7,0)
  FilletRadius = 0
  Length = 0.5
  MakeFace = false
  Placement = pos=(35.5,-60,0) rot=(0,0,1;0rad)
  Points = (2) [(-188.5,-1.2,0),(-188.5,-1.7,0)]
  Start = (-153,-61.2,0)
  Subdivisions = 0
FEATURE [Part::Part2DObjectPython] Line165  # Draft 2D object (typed FeaturePython)
  Area = 0
  ChamferSize = 0
  Closed = true
  End = (-149.1,-61.2,0)
  FilletRadius = 0
  Length = 2.9
  MakeFace = false
  Placement = pos=(35.5,-60,0) rot=(0,0,1;0rad)
  Points = (2) [(-187.5,-1.2,0),(-184.6,-1.2,0)]
  Start = (-152,-61.2,0)
  Subdivisions = 0
FEATURE [Part::Part2DObjectPython] Line166  # Draft 2D object (typed FeaturePython)
  Area = 0
  ChamferSize = 0
  Closed = true
  End = (-149.1,-62.2,0)
  FilletRadius = 0
  Length = 3.4
  MakeFace = false
  Placement = pos=(35.5,-60,0) rot=(0,0,1;0rad)
  Points = (2) [(-188,-2.2,0),(-184.6,-2.2,0)]
  Start = (-152.5,-62.2,0)
  Subdivisions = 0
FEATURE [Part::Part2DObjectPython] Line167  # Draft 2D object (typed FeaturePython)
  Area = 0
  ChamferSize = 0
  Closed = false
  End = (-149.2,-64.7,0)
  FilletRadius = 0
  Length = 0.1
  MakeFace = false
  Placement = pos=(35.5,-60,0) rot=(0,0,1;0rad)
  Points = (2) [(-184.6,-4.7,0),(-184.7,-4.7,0)]
  Start = (-149.1,-64.7,0)
  Subdivisions = 0
FEATURE [Part::Part2DObjectPython] Line168  # Draft 2D object (typed FeaturePython)
  Area = 0
  ChamferSize = 0
  Closed = false
  End = (-149.1,-64.7,0)
  FilletRadius = 0
  Length = 0.303
  MakeFace = false
  Placement = pos=(35.5,-60,0) rot=(0,0,1;0rad)
  Points = (2) [(-184.297,-4.7,0),(-184.6,-4.7,0)]
  Start = (-148.797,-64.7,0)
  Subdivisions = 0
FEATURE [Part::Part2DObjectPython] Line169  # Draft 2D object (typed FeaturePython)
  Area = 0
  ChamferSize = 0
  Closed = false
  End = (-149.1,-58.7,0)
  FilletRadius = 0
  Length = 0.303
  MakeFace = false
  Placement = pos=(35.5,-60,0) rot=(0,0,1;0rad)
  Points = (2) [(-184.297,1.3,0),(-184.6,1.3,0)]
  Start = (-148.797,-58.7,0)
  Subdivisions = 0
FEATURE [Part::Part2DObjectPython] Line170  # Draft 2D object (typed FeaturePython)
  Area = 0
  ChamferSize = 0
  Closed = false
  End = (-155.8,-58.7,0)
  FilletRadius = 0
  Length = 0.1
  MakeFace = false
  Placement = pos=(35.5,-60,0) rot=(0,0,1;0rad)
  Points = (2) [(-191.4,1.3,0),(-191.3,1.3,0)]
  Start = (-155.9,-58.7,0)
  Subdivisions = 0
FEATURE [Part::Part2DObjectPython] Line171  # Draft 2D object (typed FeaturePython)
  Area = 0
  ChamferSize = 0
  Closed = false
  End = (-149.2,-58.7,0)
  FilletRadius = 0
  Length = 0.1
  MakeFace = false
  Placement = pos=(35.5,-60,0) rot=(0,0,1;0rad)
  Points = (2) [(-184.6,1.3,0),(-184.7,1.3,0)]
  Start = (-149.1,-58.7,0)
  Subdivisions = 0
FEATURE [Part::Part2DObjectPython] Line172  # Draft 2D object (typed FeaturePython)
  Area = 0
  ChamferSize = 0
  Closed = false
  End = (-156.203,-64.7,0)
  FilletRadius = 0
  Length = 0.303
  MakeFace = false
  Placement = pos=(35.5,-60,0) rot=(0,0,1;0rad)
  Points = (2) [(-191.4,-4.7,0),(-191.703,-4.7,0)]
  Start = (-155.9,-64.7,0)
  Subdivisions = 0
FEATURE [Part::Part2DObjectPython] Line173  # Draft 2D object (typed FeaturePython)
  Area = 0
  ChamferSize = 0
  Closed = false
  End = (-155.8,-64.7,0)
  FilletRadius = 0
  Length = 0.1
  MakeFace = false
  Placement = pos=(35.5,-60,0) rot=(0,0,1;0rad)
  Points = (2) [(-191.4,-4.7,0),(-191.3,-4.7,0)]
  Start = (-155.9,-64.7,0)
  Subdivisions = 0
FEATURE [Part::Part2DObjectPython] Line174  # Draft 2D object (typed FeaturePython)
  Area = 0
  ChamferSize = 0
  Closed = false
  End = (-156.203,-58.7,0)
  FilletRadius = 0
  Length = 0.303
  MakeFace = false
  Placement = pos=(35.5,-60,0) rot=(0,0,1;0rad)
  Points = (2) [(-191.4,1.3,0),(-191.703,1.3,0)]
  Start = (-155.9,-58.7,0)
  Subdivisions = 0
FEATURE [Part::Part2DObjectPython] Line175  # Draft 2D object (typed FeaturePython)
  Area = 0
  ChamferSize = 0
  Closed = false
  End = (-114.75,-28.6,0)
  FilletRadius = 0
  Length = 25.25
  MakeFace = false
  Placement = pos=(-75,-40,0) rot=(0,0,1;0rad)
  Points = (2) [(-65,11.4,0),(-39.75,11.4,0)]
  Start = (-140,-28.6,0)
  Subdivisions = 0
FEATURE [Part::Part2DObjectPython] Line176  # Draft 2D object (typed FeaturePython)
  Area = 0
  ChamferSize = 0
  Closed = false
  End = (-114.75,-27.3,0)
  FilletRadius = 0
  Length = 25.25
  MakeFace = false
  Placement = pos=(-75,-40,0) rot=(0,0,1;0rad)
  Points = (2) [(-65,12.7,0),(-39.75,12.7,0)]
  Start = (-140,-27.3,0)
  Subdivisions = 0
FEATURE [App::FeaturePython] Text  # WARN: FeaturePython — macro-defined, semantics opaque (R4)
  Placement = pos=(-175,50,0) rot=(0,0,1;0rad)
  Text = MHD-1
FEATURE [Part::FeaturePython] Hatch  # WARN: FeaturePython — macro-defined, semantics opaque (R4)
  File = C:/Program Files/FreeCAD 0.21/data/Mod/TechDraw/PAT/FCPAT.pat
  Pattern = Diagonal4
  Rotation = 0
  Scale = 0.5
  Translate = true
FEATURE [Part::FeaturePython] Hatch001  # WARN: FeaturePython — macro-defined, semantics opaque (R4)
  File = C:/Program Files/FreeCAD 0.21/data/Mod/TechDraw/PAT/FCPAT.pat
  Pattern = Diagonal4
  Rotation = 0
  Scale = 0.5
  Translate = true
FEATURE [Part::Part2DObjectPython] Line177  # Draft 2D object (typed FeaturePython)
  Area = 0
  ChamferSize = 0
  Closed = true
  End = (33.9,-40,0)
  FilletRadius = 0
  Length = 18.4
  MakeFace = false
  Placement = pos=(35.5,-60,0) rot=(0,0,1;0rad)
  Points = (2) [(-1.6,1.6,0),(-1.6,20,0)]
  Start = (33.9,-58.4,0)
  Subdivisions = 0
FEATURE [Part::FeaturePython] Hatch002  # WARN: FeaturePython — macro-defined, semantics opaque (R4)
  File = C:/Program Files/FreeCAD 0.21/data/Mod/TechDraw/PAT/FCPAT.pat
  Pattern = Diagonal4
  Rotation = 0
  Scale = 0.5
  Translate = true
FEATURE [Part::Part2DObjectPython] Line178  # Draft 2D object (typed FeaturePython)
  Area = 0
  ChamferSize = 0
  Closed = true
  End = (36.1,-40,0)
  FilletRadius = 0
  Length = 18.4
  MakeFace = false
  Placement = pos=(35.5,-60,0) rot=(0,0,1;0rad)
  Points = (2) [(0.6,1.6,0),(0.6,20,0)]
  Start = (36.1,-58.4,0)
  Subdivisions = 0
FEATURE [Part::Part2DObjectPython] Line179  # Draft 2D object (typed FeaturePython)
  Area = 0
  ChamferSize = 0
  Closed = true
  End = (73.9,-40,0)
  FilletRadius = 0
  Length = 18.4
  MakeFace = false
  Placement = pos=(35.5,-60,0) rot=(0,0,1;0rad)
  Points = (2) [(38.4,1.6,0),(38.4,20,0)]
  Start = (73.9,-58.4,0)
  Subdivisions = 0
FEATURE [Part::FeaturePython] Hatch003  # WARN: FeaturePython — macro-defined, semantics opaque (R4)
  File = C:/Program Files/FreeCAD 0.21/data/Mod/TechDraw/PAT/FCPAT.pat
  Pattern = Diagonal4
  Rotation = 0
  Scale = 0.5
  Translate = true
FEATURE [Part::Feature] Wire002
  shape: bbox 37.8 x 30.9 x 2e-07 mm, 0 faces, 0 solids (baked)
FEATURE [Part::Part2DObjectPython] Line183  # Draft 2D object (typed FeaturePython)
  Area = 0
  ChamferSize = 0
  Closed = false
  End = (76.1,-39.9945,0)
  FilletRadius = 0
  Length = 18.4055
  MakeFace = true
  Placement = pos=(76.1,-58.4,0) rot=(-1.00615,0,0;0rad)
  Points = (2) [(0,0,0),(-1.28342e-06,18.4055,3.21813e-06)]
  Start = (76.1,-58.4,0)
  Subdivisions = 0
FEATURE [Part::FeaturePython] Hatch004  # WARN: FeaturePython — macro-defined, semantics opaque (R4)
  File = C:/Program Files/FreeCAD 0.21/data/Mod/TechDraw/PAT/FCPAT.pat
  Pattern = Diagonal5
  Rotation = 0
  Scale = 0.5
  Translate = true
FEATURE [Part::Feature] Edge
  Placement = pos=(-112.5,-30,0) rot=(0,0,1;0rad)
  shape: bbox 2e-07 x 24.8 x 2e-07 mm, 0 faces, 0 solids (baked)
FEATURE [Part::Feature] Edge001
  shape: bbox 36.4 x 2e-07 x 2e-07 mm, 0 faces, 0 solids (baked)
FEATURE [Part::Feature] Edge003
  Placement = pos=(76.1,-18,0) rot=(-1.00615,0,0;0rad)
  shape: bbox 1.483e-06 x 21.99 x 2e-07 mm, 0 faces, 0 solids (baked)
FEATURE [Part::Feature] Edge004
  Placement = pos=(75,35.31,0) rot=(0,0,1;0rad)
  shape: bbox 36.4 x 9.992 x 2e-07 mm, 0 faces, 0 solids (baked)
FEATURE [Part::Feature] Edge005
  shape: bbox 3.936e-05 x 0.002523 x 2e-07 mm, 0 faces, 0 solids (baked)
FEATURE [Part::FeaturePython] Hatch005  # WARN: FeaturePython — macro-defined, semantics opaque (R4)
  File = C:/Program Files/FreeCAD 0.21/data/Mod/TechDraw/PAT/FCPAT.pat
  Pattern = Diagonal5
  Rotation = 0
  Scale = 0.3
  Translate = true
FEATURE [Part::Feature] Wire003
  shape: bbox 11.1 x 12.8 x 2e-07 mm, 0 faces, 0 solids (baked)
FEATURE [Part::FeaturePython] Hatch006  # WARN: FeaturePython — macro-defined, semantics opaque (R4)
  File = C:/Program Files/FreeCAD 0.21/data/Mod/TechDraw/PAT/FCPAT.pat
  Pattern = Diagonal4
  Rotation = 0
  Scale = 0.5
  Translate = true
FEATURE [Part::FeaturePython] Hatch007  # WARN: FeaturePython — macro-defined, semantics opaque (R4)
  File = C:/Program Files/FreeCAD 0.21/data/Mod/TechDraw/PAT/FCPAT.pat
  Pattern = Diagonal4
  Rotation = 0
  Scale = 0.5
  Translate = true
FEATURE [Part::FeaturePython] Hatch008  # WARN: FeaturePython — macro-defined, semantics opaque (R4)
  File = C:/Program Files/FreeCAD 0.21/data/Mod/TechDraw/PAT/FCPAT.pat
  Pattern = Diamond
  Rotation = 0
  Translate = true
FEATURE [Part::Feature] Wire006
  shape: bbox 11 x 12 x 2e-07 mm, 0 faces, 0 solids (baked)
FEATURE [Part::FeaturePython] Hatch009  # WARN: FeaturePython — macro-defined, semantics opaque (R4)
  File = C:/Program Files/FreeCAD 0.21/data/Mod/TechDraw/PAT/FCPAT.pat
  Pattern = Diamond
  Rotation = 0
  Translate = true
FEATURE [Part::Feature] Wire007
  shape: bbox 38 x 12 x 2e-07 mm, 0 faces, 0 solids (baked)
FEATURE [Part::FeaturePython] Hatch010  # WARN: FeaturePython — macro-defined, semantics opaque (R4)
  File = C:/Program Files/FreeCAD 0.21/data/Mod/TechDraw/PAT/FCPAT.pat
  Pattern = Diamond
  Rotation = 0
  Translate = true
FEATURE [Part::Feature] Wire008
  shape: bbox 38 x 12 x 2e-07 mm, 0 faces, 0 solids (baked)
FEATURE [Part::Part2DObjectPython] Line092  # Draft 2D object (typed FeaturePython)
  Area = 0
  ChamferSize = 0
  Closed = false
  End = (16,24.5,0)
  FilletRadius = 0
  Length = 38
  MakeFace = false
  Placement = pos=(-70.9707,35.5939,0) rot=(0,0,1;0rad)
  Points = (2) [(48.9707,-11.0939,0),(86.9707,-11.0939,0)]
  Start = (-22,24.5,0)
  Subdivisions = 0
FEATURE [Part::Part2DObjectPython] Line086  # Draft 2D object (typed FeaturePython)
  Area = 0
  ChamferSize = 0
  Closed = true
  End = (16,35.5,0)
  FilletRadius = 0
  Length = 11
  MakeFace = false
  Placement = pos=(-157.5,-40,0) rot=(0,0,1;0rad)
  Points = (2) [(173.5,64.5,0),(173.5,75.5,0)]
  Start = (16,24.5,0)
  Subdivisions = 0
FEATURE [Part::Part2DObjectPython] Line091  # Draft 2D object (typed FeaturePython)
  Area = 0
  ChamferSize = 0
  Closed = false
  End = (16,35.5,0)
  FilletRadius = 0
  Length = 38
  MakeFace = false
  Placement = pos=(-70.9707,35.5939,0) rot=(0,0,1;0rad)
  Points = (2) [(48.9707,-0.0939102,0),(86.9707,-0.0939102,0)]
  Start = (-22,35.5,0)
  Subdivisions = 0
FEATURE [Part::Part2DObjectPython] Line085  # Draft 2D object (typed FeaturePython)
  Area = 0
  ChamferSize = 0
  Closed = true
  End = (-22,35.5,0)
  FilletRadius = 0
  Length = 11
  MakeFace = false
  Placement = pos=(-157.5,-40,0) rot=(0,0,1;0rad)
  Points = (2) [(135.5,64.5,0),(135.5,75.5,0)]
  Start = (-22,24.5,0)
  Subdivisions = 0
FEATURE [Part::Part2DObjectPython] Line186  # Draft 2D object (typed FeaturePython)
  Area = 0
  ChamferSize = 0
  Closed = false
  End = (35.5,-58.4,0)
  FilletRadius = 0
  Length = 1.6
  MakeFace = false
  Placement = pos=(35.5,-60,0) rot=(0,0,1;0rad)
  Points = (2) [(-1.6,1.6,0),(0,1.6,0)]
  Start = (33.9,-58.4,0)
  Subdivisions = 0
FEATURE [Part::Part2DObjectPython] Line187  # Draft 2D object (typed FeaturePython)
  Area = 0
  ChamferSize = 0
  Closed = false
  End = (76.1,-58.4,0)
  FilletRadius = 0
  Length = 1.6
  MakeFace = false
  Placement = pos=(35.5,-60,0) rot=(0,0,1;0rad)
  Points = (2) [(39,1.6,0),(40.6,1.6,0)]
  Start = (74.5,-58.4,0)
  Subdivisions = 0
FEATURE [Part::FeaturePython] Hatch011  # WARN: FeaturePython — macro-defined, semantics opaque (R4)
  File = C:/Program Files/FreeCAD 0.21/data/Mod/TechDraw/PAT/FCPAT.pat
  Pattern = Horizontal5
  Rotation = 22.5
  Scale = 0.2
  Translate = true
FEATURE [Part::Feature] Wire009
  shape: bbox 39 x 6.6 x 2e-07 mm, 0 faces, 0 solids (baked)
FEATURE [Part::Feature] Edge016
  shape: bbox 2e-07 x 34.04 x 2e-07 mm, 0 faces, 0 solids (baked)
FEATURE [Part::Feature] Edge017
  shape: bbox 3.5 x 2e-07 x 2e-07 mm, 0 faces, 0 solids (baked)
FEATURE [Part::Feature] Edge018
  shape: bbox 2e-07 x 29.8 x 2e-07 mm, 0 faces, 0 solids (baked)
FEATURE [Part::Feature] Edge019
  shape: bbox 2e-07 x 34.04 x 2e-07 mm, 0 faces, 0 solids (baked)
FEATURE [Part::Feature] Edge020
  shape: bbox 3.5 x 2e-07 x 2e-07 mm, 0 faces, 0 solids (baked)
FEATURE [Part::Feature] Edge021
  shape: bbox 2e-07 x 29.8 x 2e-07 mm, 0 faces, 0 solids (baked)
FEATURE [Part::FeaturePython] Hatch012  # WARN: FeaturePython — macro-defined, semantics opaque (R4)
  File = C:/Program Files/FreeCAD 0.21/data/Mod/TechDraw/PAT/FCPAT.pat
  Pattern = Vertical5
  Rotation = 22.5
  Scale = 0.1
  Translate = true
FEATURE [Part::Feature] Wire010
  shape: bbox 20 x 5 x 2e-07 mm, 0 faces, 0 solids (baked)
FEATURE [Part::Feature] Wire012
  shape: bbox 47.5 x 34.8 x 2e-07 mm, 0 faces, 0 solids (baked)
FEATURE [Part::Feature] Edge024
  Placement = pos=(35.5,-60,0) rot=(0,0,1;0rad)
  shape: bbox 2e-07 x 17 x 2e-07 mm, 0 faces, 0 solids (baked)
FEATURE [Part::Feature] Edge025
  shape: bbox 6.9 x 2e-07 x 2e-07 mm, 0 faces, 0 solids (baked)
FEATURE [Part::Feature] Edge026
  shape: bbox 2e-07 x 16.5 x 2e-07 mm, 0 faces, 0 solids (baked)
FEATURE [Part::FeaturePython] Hatch013  # WARN: FeaturePython — macro-defined, semantics opaque (R4)
  File = C:/Program Files/FreeCAD 0.21/data/Mod/TechDraw/PAT/FCPAT.pat
  Pattern = Vertical5
  Rotation = 22.5
  Scale = 0.1
  Translate = true
FEATURE [Part::Feature] Wire
  shape: bbox 105 x 0.5 x 2e-07 mm, 0 faces, 0 solids (baked)
FEATURE [Part::Part2DObjectPython] Line188  # Draft 2D object (typed FeaturePython)
  Area = 0
  ChamferSize = 0
  Closed = true
  End = (30,-40,0)
  FilletRadius = 0
  Length = 3.9
  MakeFace = false
  Placement = pos=(35.5,-60,0) rot=(0,0,1;0rad)
  Points = (2) [(-1.6,20,0),(-5.5,20,0)]
  Start = (33.9,-40,0)
  Subdivisions = 0
FEATURE [Part::Part2DObjectPython] Line189  # Draft 2D object (typed FeaturePython)
  Area = 0
  ChamferSize = 0
  Closed = false
  End = (65,-6.9,0)
  FilletRadius = 0
  Length = 3
  MakeFace = false
  Points = (2) [(62,-6.9,0),(65,-6.9,0)]
  Start = (62,-6.9,0)
  Subdivisions = 0
FEATURE [Part::Part2DObjectPython] Line190  # Draft 2D object (typed FeaturePython)
  Area = 0
  ChamferSize = 0
  Closed = false
  End = (65,31.1,0)
  FilletRadius = 0
  Length = 10
  MakeFace = false
  Points = (2) [(75,31.1,0),(65,31.1,0)]
  Start = (75,31.1,0)
  Subdivisions = 0
FEATURE [Part::Part2DObjectPython] Line191  # Draft 2D object (typed FeaturePython)
  Area = 0
  ChamferSize = 0
  Closed = false
  End = (65,28.9,0)
  FilletRadius = 0
  Length = 10
  MakeFace = false
  Points = (2) [(75,28.9,0),(65,28.9,0)]
  Start = (75,28.9,0)
  Subdivisions = 0
FEATURE [Part::Part2DObjectPython] Line192  # Draft 2D object (typed FeaturePython)
  Area = 0
  ChamferSize = 0
  Closed = false
  End = (65,31.1,0)
  FilletRadius = 0
  Length = 3
  MakeFace = false
  Points = (2) [(62,31.1,0),(65,31.1,0)]
  Start = (62,31.1,0)
  Subdivisions = 0
FEATURE [Part::Part2DObjectPython] Line193  # Draft 2D object (typed FeaturePython)
  Area = 0
  ChamferSize = 0
  Closed = false
  End = (65,28.9,0)
  FilletRadius = 0
  Length = 3
  MakeFace = false
  Points = (2) [(62,28.9,0),(65,28.9,0)]
  Start = (62,28.9,0)
  Subdivisions = 0
FEATURE [Part::Part2DObjectPython] Line194  # Draft 2D object (typed FeaturePython)
  Area = 0
  ChamferSize = 0
  Closed = false
  End = (58,-8.5,0)
  FilletRadius = 0
  Length = 1
  MakeFace = false
  Points = (2) [(58,-7.5,0),(58,-8.5,0)]
  Start = (58,-7.5,0)
  Subdivisions = 0
FEATURE [Part::Part2DObjectPython] Line195  # Draft 2D object (typed FeaturePython)
  Area = 0
  ChamferSize = 0
  Closed = false
  End = (62,29.5,0)
  FilletRadius = 0
  Length = 13
  MakeFace = false
  Points = (2) [(75,29.5,0),(62,29.5,0)]
  Start = (75,29.5,0)
  Subdivisions = 0
FEATURE [Part::Part2DObjectPython] Line196  # Draft 2D object (typed FeaturePython)
  Area = 0
  ChamferSize = 0
  Closed = false
  End = (62,29.5,0)
  FilletRadius = 0
  Length = 4
  MakeFace = false
  Points = (2) [(58,29.5,0),(62,29.5,0)]
  Start = (58,29.5,0)
  Subdivisions = 0
FEATURE [Part::Part2DObjectPython] Line197  # Draft 2D object (typed FeaturePython)
  Area = 0
  ChamferSize = 0
  Closed = false
  End = (62,29.5,0)
  FilletRadius = 0
  Length = 4
  MakeFace = false
  Points = (2) [(58,29.5,0),(62,29.5,0)]
  Start = (58,29.5,0)
  Subdivisions = 0
FEATURE [Part::Part2DObjectPython] Line198  # Draft 2D object (typed FeaturePython)
  Area = 0
  ChamferSize = 0
  Closed = false
  End = (62,30.5,0)
  FilletRadius = 0
  Length = 4
  MakeFace = false
  Points = (2) [(58,30.5,0),(62,30.5,0)]
  Start = (58,30.5,0)
  Subdivisions = 0
FEATURE [Part::Part2DObjectPython] Line199  # Draft 2D object (typed FeaturePython)
  Area = 0
  ChamferSize = 0
  Closed = false
  End = (62,30.5,0)
  FilletRadius = 0
  Length = 13
  MakeFace = false
  Points = (2) [(75,30.5,0),(62,30.5,0)]
  Start = (75,30.5,0)
  Subdivisions = 0
FEATURE [Part::Part2DObjectPython] Circle005  # Draft 2D object (typed FeaturePython)
  Area = 0
  FirstAngle = 0
  LastAngle = 0
  MakeFace = false
  Placement = pos=(75,30,0) rot=(0,0,1;0rad)
  Radius = 1.1
FEATURE [Part::Part2DObjectPython] Circle006  # Draft 2D object (typed FeaturePython)
  Area = 0
  FirstAngle = 0
  LastAngle = 0
  MakeFace = false
  Placement = pos=(75,30,0) rot=(0,0,1;0rad)
  Radius = 0.5
FEATURE [Part::Part2DObjectPython] Circle007  # Draft 2D object (typed FeaturePython)
  Area = 0
  FirstAngle = 0
  LastAngle = 0
  MakeFace = false
  Placement = pos=(35,30,0) rot=(0,0,1;0rad)
  Radius = 0.5
FEATURE [Part::Part2DObjectPython] Arc028  # Draft 2D object (typed FeaturePython)
  Area = 0
  FirstAngle = -90
  LastAngle = 90
  MakeFace = true
  Placement = pos=(35,30,0) rot=(0,0,1;0rad)
  Radius = 1.1
FEATURE [Part::Part2DObjectPython] Arc029  # Draft 2D object (typed FeaturePython)
  Area = 0
  FirstAngle = 90
  LastAngle = 270
  MakeFace = false
  Placement = pos=(35,30,0) rot=(0,0,1;0rad)
  Radius = 1.1
FEATURE [Part::Part2DObjectPython] Line200  # Draft 2D object (typed FeaturePython)
  Area = 0
  ChamferSize = 0
  Closed = false
  End = (35,31.1,0)
  FilletRadius = 0
  Length = 8
  MakeFace = false
  Points = (2) [(27,31.1,0),(35,31.1,0)]
  Start = (27,31.1,0)
  Subdivisions = 0
FEATURE [Part::Part2DObjectPython] Line201  # Draft 2D object (typed FeaturePython)
  Area = 0
  ChamferSize = 0
  Closed = false
  End = (35,28.9,0)
  FilletRadius = 0
  Length = 8
  MakeFace = false
  Points = (2) [(27,28.9,0),(35,28.9,0)]
  Start = (27,28.9,0)
  Subdivisions = 0
FEATURE [Part::Part2DObjectPython] Line202  # Draft 2D object (typed FeaturePython)
  Area = 0
  ChamferSize = 0
  Closed = false
  End = (35,29.5,0)
  FilletRadius = 0
  Length = 8
  MakeFace = false
  Points = (2) [(27,29.5,0),(35,29.5,0)]
  Start = (27,29.5,0)
  Subdivisions = 0
FEATURE [Part::Part2DObjectPython] Line203  # Draft 2D object (typed FeaturePython)
  Area = 0
  ChamferSize = 0
  Closed = false
  End = (35,30.5,0)
  FilletRadius = 0
  Length = 8
  MakeFace = false
  Points = (2) [(27,30.5,0),(35,30.5,0)]
  Start = (27,30.5,0)
  Subdivisions = 0
FEATURE [Part::Part2DObjectPython] Line204  # Draft 2D object (typed FeaturePython)
  Area = 0
  ChamferSize = 0
  Closed = false
  End = (27,29.5,0)
  FilletRadius = 0
  Length = 4
  MakeFace = false
  Points = (2) [(23,29.5,0),(27,29.5,0)]
  Start = (23,29.5,0)
  Subdivisions = 0
FEATURE [Part::Part2DObjectPython] Line205  # Draft 2D object (typed FeaturePython)
  Area = 0
  ChamferSize = 0
  Closed = false
  End = (27,30.5,0)
  FilletRadius = 0
  Length = 4
  MakeFace = false
  Points = (2) [(23,30.5,0),(27,30.5,0)]
  Start = (23,30.5,0)
  Subdivisions = 0
FEATURE [Part::Part2DObjectPython] Line206  # Draft 2D object (typed FeaturePython)
  Area = 0
  ChamferSize = 0
  Closed = false
  End = (23,29.5,0)
  FilletRadius = 0
  Length = 1
  MakeFace = false
  Points = (2) [(23,30.5,0),(23,29.5,0)]
  Start = (23,30.5,0)
  Subdivisions = 0
FEATURE [Part::Part2DObjectPython] Line207  # Draft 2D object (typed FeaturePython)
  Area = 0
  ChamferSize = 0
  Closed = false
  End = (35.5,26.7,0)
  FilletRadius = 0
  Length = 6.6
  MakeFace = false
  Points = (2) [(35.5,33.3,0),(35.5,26.7,0)]
  Start = (35.5,33.3,0)
  Subdivisions = 0
FEATURE [Part::Part2DObjectPython] Line208  # Draft 2D object (typed FeaturePython)
  Area = 0
  ChamferSize = 0
  Closed = false
  End = (35.5,26.7,0)
  FilletRadius = 0
  Length = 39
  MakeFace = false
  Points = (2) [(74.5,26.7,0),(35.5,26.7,0)]
  Start = (74.5,26.7,0)
  Subdivisions = 0
FEATURE [Part::Part2DObjectPython] Line209  # Draft 2D object (typed FeaturePython)
  Area = 0
  ChamferSize = 0
  Closed = false
  End = (74.5,26.7,0)
  FilletRadius = 0
  Length = 6.6
  MakeFace = false
  Points = (2) [(74.5,33.3,0),(74.5,26.7,0)]
  Start = (74.5,33.3,0)
  Subdivisions = 0
FEATURE [Part::Part2DObjectPython] Line210  # Draft 2D object (typed FeaturePython)
  Area = 0
  ChamferSize = 0
  Closed = false
  End = (35.5,33.3,0)
  FilletRadius = 0
  Length = 39
  MakeFace = false
  Points = (2) [(74.5,33.3,0),(35.5,33.3,0)]
  Start = (74.5,33.3,0)
  Subdivisions = 0
FEATURE [Part::Part2DObjectPython] Arc030  # Draft 2D object (typed FeaturePython)
  Area = 0
  FirstAngle = 90
  LastAngle = 180
  MakeFace = true
  Placement = pos=(35,33.8,0) rot=(0,0,1;0rad)
  Radius = 0.5
FEATURE [Part::Part2DObjectPython] Line211  # Draft 2D object (typed FeaturePython)
  Area = 0
  ChamferSize = 0
  Closed = false
  End = (34.5,30,0)
  FilletRadius = 0
  Length = 3.8
  MakeFace = false
  Points = (2) [(34.5,33.8,0),(34.5,30,0)]
  Start = (34.5,33.8,0)
  Subdivisions = 0
FEATURE [Part::Part2DObjectPython] Line212  # Draft 2D object (typed FeaturePython)
  Area = 0
  ChamferSize = 0
  Closed = true
  End = (38.5,26.7,0)
  FilletRadius = 0
  Length = 1
  MakeFace = false
  Placement = pos=(35.5,-60,0) rot=(0,0,1;0rad)
  Points = (2) [(3,85.7,0),(3,86.7,0)]
  Start = (38.5,25.7,0)
  Subdivisions = 0
FEATURE [Part::Part2DObjectPython] Line  # Draft 2D object (typed FeaturePython)
  Area = 0
  ChamferSize = 0
  Closed = false
  End = (71.5,34.3,0)
  FilletRadius = 0
  Length = 36.5
  MakeFace = true
  Placement = pos=(35,34.3,0) rot=(0,0,1;0rad)
  Points = (2) [(0,0,0),(36.5,0,0)]
  Start = (35,34.3,0)
  Subdivisions = 0
FEATURE [Part::Part2DObjectPython] Arc031  # Draft 2D object (typed FeaturePython)
  Area = 0
  FirstAngle = -90
  LastAngle = 0
  MakeFace = true
  Placement = pos=(75,26.2,0) rot=(0,0,1;0rad)
  Radius = 0.5
FEATURE [Part::Part2DObjectPython] Line213  # Draft 2D object (typed FeaturePython)
  Area = 0
  ChamferSize = 0
  Closed = true
  End = (71.5,33.3,0)
  FilletRadius = 0
  Length = 1
  MakeFace = false
  Placement = pos=(35.5,-60,0) rot=(0,0,1;0rad)
  Points = (2) [(36,94.3,0),(36,93.3,0)]
  Start = (71.5,34.3,0)
  Subdivisions = 0
FEATURE [Part::Part2DObjectPython] Line214  # Draft 2D object (typed FeaturePython)
  Area = 0
  ChamferSize = 0
  Closed = false
  End = (75.5,26.2,0)
  FilletRadius = 0
  Length = 3.8
  MakeFace = true
  Placement = pos=(75.5,30,0) rot=(0,0,1;0rad)
  Points = (2) [(0,0,0),(0,-3.8,0)]
  Start = (75.5,30,0)
  Subdivisions = 0
FEATURE [Part::Part2DObjectPython] Line215  # Draft 2D object (typed FeaturePython)
  Area = 0
  ChamferSize = 0
  Closed = false
  End = (75,25.7,0)
  FilletRadius = 0
  Length = 36.5
  MakeFace = true
  Placement = pos=(36.5,25.7,0) rot=(0,0,1;0rad)
  Points = (2) [(2,-3.55271e-15,0),(38.5,-3.55271e-15,0)]
  Start = (38.5,25.7,0)
  Subdivisions = 0
FEATURE [Part::Part2DObjectPython] Line216  # Draft 2D object (typed FeaturePython)
  Area = 0
  ChamferSize = 0
  Closed = true
  End = (37.5,26.7,0)
  FilletRadius = 0
  Length = 2.1
  MakeFace = false
  Placement = pos=(35.5,-60,0) rot=(0,0,1;0rad)
  Points = (2) [(2,84.6,0),(2,86.7,0)]
  Start = (37.5,24.6,0)
  Subdivisions = 0
FEATURE [Part::Part2DObjectPython] Line217  # Draft 2D object (typed FeaturePython)
  Area = 0
  ChamferSize = 0
  Closed = true
  End = (72.5,26.7,0)
  FilletRadius = 0
  Length = 2.1
  MakeFace = false
  Placement = pos=(35.5,-60,0) rot=(0,0,1;0rad)
  Points = (2) [(37,84.6,0),(37,86.7,0)]
  Start = (72.5,24.6,0)
  Subdivisions = 0
FEATURE [Part::Part2DObjectPython] Line218  # Draft 2D object (typed FeaturePython)
  Area = 0
  ChamferSize = 0
  Closed = true
  End = (72.5,33.3,0)
  FilletRadius = 0
  Length = 2.1
  MakeFace = false
  Placement = pos=(35.5,-60,0) rot=(0,0,1;0rad)
  Points = (2) [(37,95.4,0),(37,93.3,0)]
  Start = (72.5,35.4,0)
  Subdivisions = 0
FEATURE [Part::Part2DObjectPython] Line219  # Draft 2D object (typed FeaturePython)
  Area = 0
  ChamferSize = 0
  Closed = true
  End = (37.5,33.3,0)
  FilletRadius = 0
  Length = 2.1
  MakeFace = false
  Placement = pos=(35.5,-60,0) rot=(0,0,1;0rad)
  Points = (2) [(2,95.4,0),(2,93.3,0)]
  Start = (37.5,35.4,0)
  Subdivisions = 0
FEATURE [Part::Part2DObjectPython] Line220  # Draft 2D object (typed FeaturePython)
  Area = 0
  ChamferSize = 0
  Closed = false
  End = (72.5,35.4,0)
  FilletRadius = 0
  Length = 35
  MakeFace = true
  Placement = pos=(37.5,35.4,0) rot=(0,0,1;0rad)
  Points = (2) [(0,0,0),(35,0,0)]
  Start = (37.5,35.4,0)
  Subdivisions = 0
FEATURE [Part::Part2DObjectPython] Line221  # Draft 2D object (typed FeaturePython)
  Area = 0
  ChamferSize = 0
  Closed = false
  End = (72.5,24.6,0)
  FilletRadius = 0
  Length = 35
  MakeFace = true
  Placement = pos=(37.5,24.6,0) rot=(0,0,1;0rad)
  Points = (2) [(0,0,0),(35,0,0)]
  Start = (37.5,24.6,0)
  Subdivisions = 0
FEATURE [App::FeaturePython] dLabel  # WARN: FeaturePython — macro-defined, semantics opaque (R4)
  CustomText = Label
  LabelType = 0
  Placement = pos=(-145.5,-72.25,0) rot=(0,0,1;1.5708rad)
  Points = (3) [(-145.5,-72.25,0),(-149.5,-72.25,0),(-152.5,-72.25,0)]
  StraightDirection = 1
  StraightDistance = 4
  TargetPoint = (-152.5,-72.25,0)
  Text = Label
FEATURE [Part::Part2DObjectPython] Line222  # Draft 2D object (typed FeaturePython)
  Area = 0
  ChamferSize = 0
  Closed = false
  End = (-115,30,6e-16)
  FilletRadius = 0
  Length = 10
  MakeFace = true
  Placement = pos=(-125,30,0) rot=(0,0,1;0rad)
  Points = (2) [(0,0,0),(10,0,6.12323e-16)]
  Start = (-125,30,0)
  Subdivisions = 0
FEATURE [App::FeaturePython] dLabel001  # WARN: FeaturePython — macro-defined, semantics opaque (R4)
  CustomText = Label
  LabelType = 0
  Placement = pos=(120,23,0) rot=(0,0,1;0rad)
  Points = (3) [(120,23,0),(120,27,0),(120,30,0)]
  StraightDirection = 1
  StraightDistance = 4
  TargetPoint = (120,30,0)
  Text = Label
  expr: .Placement.Base.x = 120 mm
FEATURE [Part::Part2DObjectPython] Line223  # Draft 2D object (typed FeaturePython)
  Area = 0
  ChamferSize = 0
  Closed = false
  End = (115,30,6e-16)
  FilletRadius = 0
  Length = 10
  MakeFace = true
  Placement = pos=(-125,30,0) rot=(0,0,1;0rad)
  Points = (2) [(250,0,0),(240,0,6e-16)]
  Start = (125,30,0)
  Subdivisions = 0
FEATURE [Part::Part2DObjectPython] Line224  # Draft 2D object (typed FeaturePython)
  Area = 0
  ChamferSize = 0
  Closed = false
  End = (1.2e-15,17.75,1.2e-15)
  FilletRadius = 0
  Length = 20
  MakeFace = true
  Placement = pos=(0,-2.25,0) rot=(0,0,1;0rad)
  Points = (2) [(0,0,0),(1.22465e-15,20,1.22465e-15)]
  Start = (0,-2.25,0)
  Subdivisions = 0
FEATURE [Part::Part2DObjectPython] Line225  # Draft 2D object (typed FeaturePython)
  Area = 0
  ChamferSize = 0
  Closed = false
  End = (1.2e-15,-42.25,1.2e-15)
  FilletRadius = 0
  Length = 30
  MakeFace = true
  Placement = pos=(0,-2.25,0) rot=(0,0,1;0rad)
  Points = (2) [(0,-70,0),(1.2e-15,-40,1.2e-15)]
  Start = (0,-72.25,0)
  Subdivisions = 0
FEATURE [Part::Part2DObjectPython] Line226  # Draft 2D object (typed FeaturePython)
  Area = 0
  ChamferSize = 0
  Closed = false
  End = (1.2e-15,52.75,1.2e-15)
  FilletRadius = 0
  Length = 10.5
  MakeFace = true
  Placement = pos=(0,-2.25,0) rot=(0,0,1;0rad)
  Points = (2) [(0,44.5,0),(1.2e-15,55,1.2e-15)]
  Start = (0,42.25,0)
  Subdivisions = 0
FEATURE [Part::Part2DObjectPython] Line227  # Draft 2D object (typed FeaturePython)
  Area = 0
  ChamferSize = 0
  Closed = false
  End = (-152.5,-67.25,1.2e-15)
  FilletRadius = 0
  Length = 10
  MakeFace = true
  Placement = pos=(0,-2.25,0) rot=(0,0,1;0rad)
  Points = (2) [(-152.5,-75,0),(-152.5,-65,1.2e-15)]
  Start = (-152.5,-77.25,0)
  Subdivisions = 0
FEATURE [Part::Part2DObjectPython] Line228  # Draft 2D object (typed FeaturePython)
  Area = 0
  ChamferSize = 0
  Closed = false
  End = (-152.5,7.25,1.2e-15)
  FilletRadius = 0
  Length = 9.5
  MakeFace = true
  Placement = pos=(0,-2.25,0) rot=(0,0,1;0rad)
  Points = (2) [(-152.5,0,0),(-152.5,9.5,1.2e-15)]
  Start = (-152.5,-2.25,0)
  Subdivisions = 0
FEATURE [App::FeaturePython] dLabel002  # WARN: FeaturePython — macro-defined, semantics opaque (R4)
  CustomText = Label
  LabelType = 0
  Placement = pos=(-120,23,0) rot=(0,0,1;0rad)
  Points = (3) [(-120,23,0),(-120,27,0),(-120,30,0)]
  StraightDirection = 1
  StraightDistance = 4
  TargetPoint = (-120,30,0)
  Text = Label
FEATURE [App::FeaturePython] dLabel003  # WARN: FeaturePython — macro-defined, semantics opaque (R4)
  CustomText = Label
  LabelType = 0
  Placement = pos=(-145.5,2.25,0) rot=(0,0,1;1.5708rad)
  Points = (3) [(-145.5,2.25,0),(-149.5,2.25,0),(-152.5,2.25,0)]
  StraightDirection = 1
  StraightDistance = 4
  TargetPoint = (-152.5,2.25,0)
  Text = Label
FEATURE [App::FeaturePython] Dimension  # Draft dimension (typed FeaturePython)
  Diameter = false
  Dimline = (-160.75,-48,0)
  Direction = (0,0,0)
  Distance = 3
  End = (-72,-5.2,0)
  Normal = (0,0,1)
  Start = (-75,-5.2,0)
FEATURE [App::FeaturePython] Dimension001  # Draft dimension (typed FeaturePython)
  Diameter = false
  Dimline = (-92.75,47.5,0)
  Direction = (0,0,0)
  Distance = 37.5
  End = (-75,-5.2,0)
  Normal = (0,0,1)
  Start = (-112.5,-5.2,0)
FEATURE [App::FeaturePython] Dimension002  # Draft dimension (typed FeaturePython)
  Diameter = false
  Dimline = (92.75,47.5,0)
  Direction = (0,0,0)
  Distance = 37.5
  End = (112.5,-5.2,0)
  Normal = (0,0,1)
  Start = (75,-5.2,0)
FEATURE [App::FeaturePython] Dimension003  # Draft dimension (typed FeaturePython)
  Diameter = false
  Dimline = (-92.75,55,0)
  Direction = (0,0,0)
  Distance = 225
  End = (112.5,-5.2,0)
  Normal = (0,0,1)
  Start = (-112.5,-5.2,0)
FEATURE [App::FeaturePython] Dimension004  # Draft dimension (typed FeaturePython)
  Diameter = false
  Dimline = (-160.75,20,0)
  Direction = (0,0,0)
  Distance = 20
  End = (-142.5,-5.2,0)
  Normal = (0,0,1)
  Start = (-162.5,-5.2,0)
FEATURE [App::FeaturePython] dLabel004  # WARN: FeaturePython — macro-defined, semantics opaque (R4)
  CustomText = Label
  LabelType = 0
  Placement = pos=(-7,-67.25,0) rot=(0,0,1;-1.5708rad)
  Points = (3) [(-7,-67.25,0),(-3,-67.25,0),(0,-67.25,0)]
  StraightDirection = 1
  StraightDistance = 4
  TargetPoint = (0,-67.25,0)
  Text = Label
FEATURE [App::FeaturePython] dLabel005  # WARN: FeaturePython — macro-defined, semantics opaque (R4)
  CustomText = Label
  LabelType = 0
  Placement = pos=(-7,47.5,0) rot=(0,0,1;-1.5708rad)
  Points = (3) [(-7,47.5,0),(-3,47.5,0),(0,47.5,0)]
  StraightDirection = 1
  StraightDistance = 4
  TargetPoint = (0,47.5,0)
  Text = Label
FEATURE [App::FeaturePython] Dimension005  # Draft dimension (typed FeaturePython)
  Diameter = false
  Dimline = (-92.75,-75,0)
  Direction = (0,0,0)
  Distance = 105
  End = (30,-5.2,0)
  Normal = (0,0,1)
  Start = (-75,-5.2,0)
FEATURE [App::FeaturePython] Dimension006  # Draft dimension (typed FeaturePython)
  Diameter = false
  Dimline = (-92.75,-75,0)
  Direction = (0,0,0)
  Distance = 37.5
  End = (-75,-5.2,0)
  Normal = (0,0,1)
  Start = (-112.5,-5.2,0)
FEATURE [App::FeaturePython] Dimension007  # Draft dimension (typed FeaturePython)
  Diameter = false
  Dimline = (-92.75,-75,0)
  Direction = (0,0,0)
  Distance = 5
  End = (35,-5.2,0)
  Normal = (0,0,1)
  Start = (30,-5.2,0)
FEATURE [App::FeaturePython] Dimension008  # Draft dimension (typed FeaturePython)
  Diameter = false
  Dimline = (-92.75,-75,0)
  Direction = (0,0,0)
  Distance = 37.5
  End = (112.5,-5.2,0)
  Normal = (0,0,1)
  Start = (75,-5.2,0)
FEATURE [App::FeaturePython] dLabel006  # WARN: FeaturePython — macro-defined, semantics opaque (R4)
  CustomText = Label
  LabelType = 0
  Placement = pos=(-7,7.5,0) rot=(0,0,1;-1.5708rad)
  Points = (3) [(-7,7.5,0),(-3,7.5,0),(0,7.5,0)]
  StraightDirection = 1
  StraightDistance = 4
  TargetPoint = (0,7.5,0)
  Text = Label
FEATURE [App::FeaturePython] Dimension009  # Draft dimension (typed FeaturePython)
  Diameter = false
  Dimline = (-160.75,12.5,0)
  Direction = (0,0,0)
  Distance = 3.5
  End = (-159,-5.2,0)
  Normal = (0,0,1)
  Start = (-162.5,-5.2,0)
FEATURE [App::FeaturePython] dLabel007  # WARN: FeaturePython — macro-defined, semantics opaque (R4)
  CustomText = Brine | Waterline
  LabelType = 0
  Placement = pos=(-127.5,-40,0) rot=(0,0,1;0rad)
  Points = (3) [(-127.5,-40,0),(-127.5,-36,0),(-127.5,-28.6,0)]
  StraightDirection = 1
  StraightDistance = 4
  TargetPoint = (-127.5,-28.6,0)
  Text = Brine | Waterline
FEATURE [App::FeaturePython] dLabel008  # WARN: FeaturePython — macro-defined, semantics opaque (R4)
  CustomText = Seawater | Waterline
  LabelType = 0
  Placement = pos=(-127.5,-15,0) rot=(0,0,1;0rad)
  Points = (3) [(-127.5,-15,0),(-127.5,-19,0),(-127.5,-27.3,0)]
  StraightDirection = 1
  StraightDistance = -4
  TargetPoint = (-127.5,-27.3,0)
  Text = Seawater | Waterline
FEATURE [App::FeaturePython] Dimension010  # Draft dimension (typed FeaturePython)
  Diameter = false
  Dimline = (-160.75,-48,0)
  Direction = (0,0,0)
  Distance = 3
  End = (30,-5.2,0)
  Normal = (0,0,1)
  Start = (27,-5.2,0)
FEATURE [App::FeaturePython] Text001  # WARN: FeaturePython — macro-defined, semantics opaque (R4)
  Placement = pos=(-175,42,0) rot=(0,0,1;0rad)
  Text = G. Quénot
FEATURE [App::FeaturePython] Dimension011  # Draft dimension (typed FeaturePython)
  Diameter = false
  Dimline = (122.5,-75,0)
  Direction = (0,0,0)
  Distance = 25
  End = (112.5,-5,0)
  Normal = (0,0,1)
  Start = (112.5,-30,0)
FEATURE [App::FeaturePython] Dimension012  # Draft dimension (typed FeaturePython)
  Diameter = false
  Dimline = (-172.5,-75,0)
  Direction = (0,0,0)
  Distance = 60
  End = (112.5,-5,0)
  Normal = (0,0,1)
  Start = (112.5,-65,0)
FEATURE [App::FeaturePython] Dimension013  # Draft dimension (typed FeaturePython)
  Diameter = false
  Dimline = (85.5,-75,0)
  Direction = (0,0,0)
  Distance = 18.4
  End = (75,-40,0)
  Normal = (0,0,1)
  Start = (75,-58.4,0)
FEATURE [App::FeaturePython] Dimension014  # Draft dimension (typed FeaturePython)
  Diameter = false
  Dimline = (122.5,-75,0)
  Direction = (0,0,0)
  Distance = 10
  End = (112.5,-30,0)
  Normal = (0,0,1)
  Start = (112.5,-40,0)
FEATURE [App::FeaturePython] Dimension015  # Draft dimension (typed FeaturePython)
  Diameter = false
  Dimline = (122.5,-75,0)
  Direction = (0,0,0)
  Distance = 25
  End = (75,-40,0)
  Normal = (0,0,1)
  Start = (75,-65,0)
FEATURE [App::FeaturePython] Dimension016  # Draft dimension (typed FeaturePython)
  Diameter = false
  Dimline = (85.5,-75,0)
  Direction = (0,0,0)
  Distance = 6.6
  End = (75,-58.4,0)
  Normal = (0,0,1)
  Start = (75,-65,0)
FEATURE [App::FeaturePython] Dimension017  # Draft dimension (typed FeaturePython)
  Diameter = false
  Dimline = (-92.75,47.5,0)
  Direction = (0,0,0)
  Distance = 10
  End = (75,-5.2,0)
  Normal = (0,0,1)
  Start = (65,-5.2,0)
FEATURE [App::FeaturePython] Dimension018  # Draft dimension (typed FeaturePython)
  Diameter = false
  Dimline = (-92.75,47.5,0)
  Direction = (0,0,0)
  Distance = 10
  End = (-65,-5.2,0)
  Normal = (0,0,1)
  Start = (-75,-5.2,0)
FEATURE [Part::Part2DObjectPython] Line230  # Draft 2D object (typed FeaturePython)
  Area = 0
  ChamferSize = 0
  Closed = false
  End = (-112.5,-32.5,0)
  FilletRadius = 0
  Length = 32.5
  MakeFace = false
  Placement = pos=(-75,-40,0) rot=(0,0,1;0rad)
  Points = (2) [(-37.5,-25,0),(-37.5,7.5,0)]
  Start = (-112.5,-65,0)
  Subdivisions = 0
FEATURE [Part::Part2DObjectPython] Line231  # Draft 2D object (typed FeaturePython)
  Area = 0
  ChamferSize = 0
  Closed = false
  End = (112.5,-32.5,0)
  FilletRadius = 0
  Length = 37.5
  MakeFace = false
  Placement = pos=(-75,-40,0) rot=(0,0,1;0rad)
  Points = (2) [(187.5,-30,0),(187.5,7.5,0)]
  Start = (112.5,-70,0)
  Subdivisions = 0
FEATURE [Part::Part2DObjectPython] Line232  # Draft 2D object (typed FeaturePython)
  Area = 0
  ChamferSize = 0
  Closed = false
  End = (-159,-65,0)
  FilletRadius = 0
  Length = 11
  MakeFace = false
  Placement = pos=(-75,-40,0) rot=(0,0,1;0rad)
  Points = (2) [(-95,-25,0),(-84,-25,0)]
  Start = (-170,-65,0)
  Subdivisions = 0
FEATURE [App::FeaturePython] Dimension019  # Draft dimension (typed FeaturePython)
  Diameter = false
  Dimline = (-92.75,-75,0)
  Direction = (0,0,0)
  Distance = 40
  End = (75,-5.2,0)
  Normal = (0,0,1)
  Start = (35,-5.2,0)
